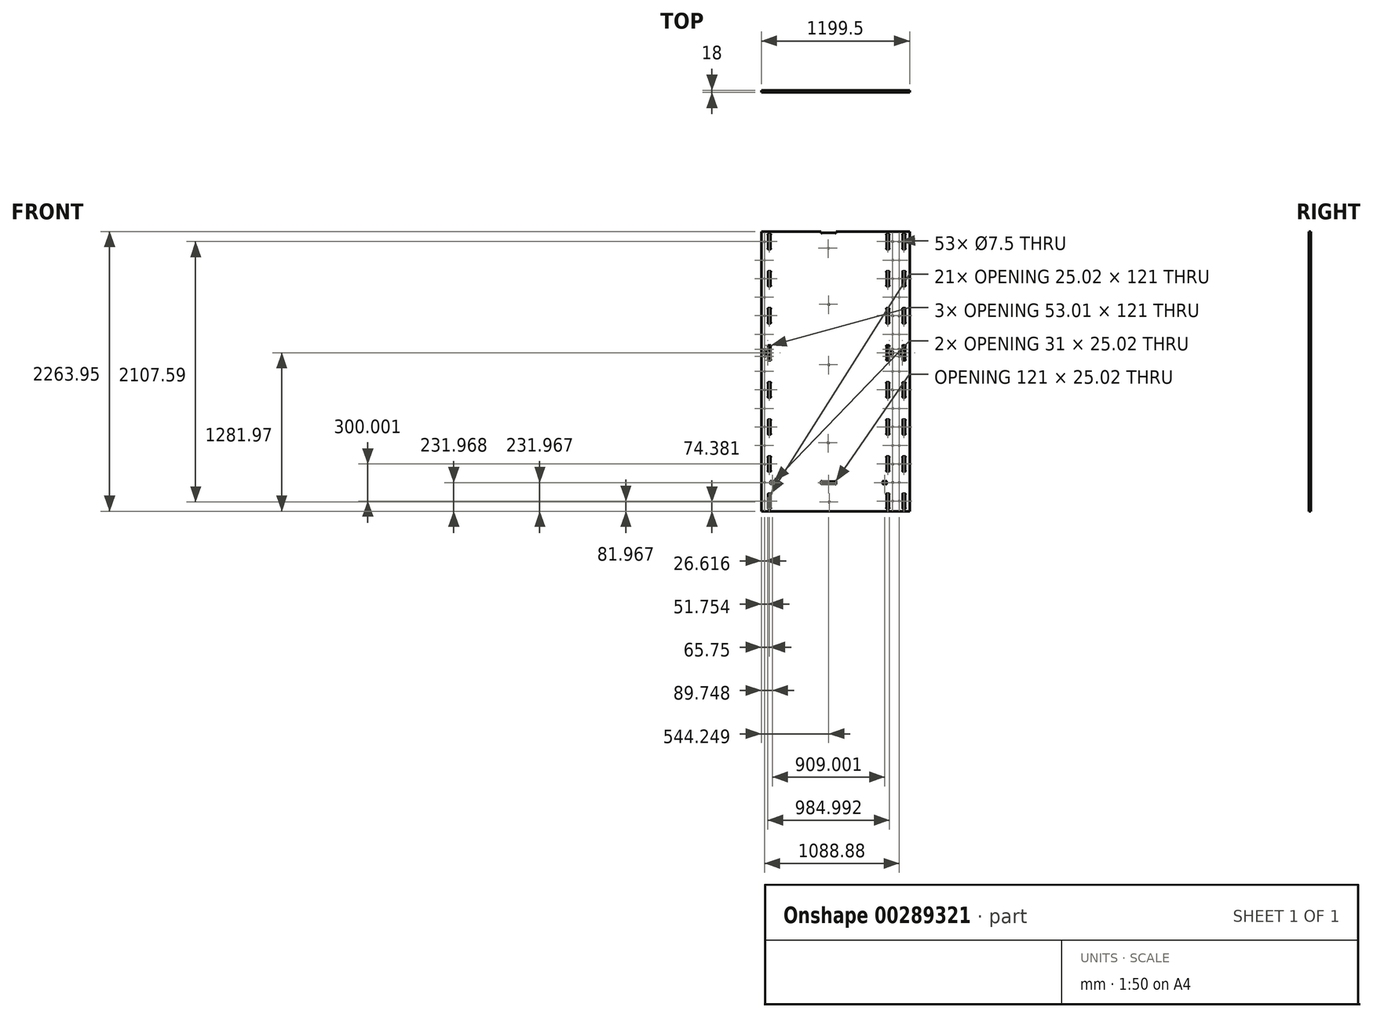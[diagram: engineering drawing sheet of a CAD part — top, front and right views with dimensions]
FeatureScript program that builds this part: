
annotation { "Feature Type Name" : "Feature", "Feature Type Description" : "" }
export const myFeature = defineFeature(function(context is Context, id is Id, definition is map)
    precondition{}
    {
        {
            var Q0;
            Q0=qCreatedBy(makeId("Front.planeOp"),FACE);
            var sketch = newSketch(context, id + "F0", { "sketchPlane" : qUnion([Q0])});
            skLineSegment(sketch, "E0", {"start": v(-600, -1200) * mm, "end": v(600, -1200) * mm});
            skLineSegment(sketch, "E1", {"start": v(600, -1200) * mm, "end": v(600, 1200) * mm});
            skLineSegment(sketch, "E2", {"start": v(600, 1200) * mm, "end": v(-600, 1200) * mm});
            skLineSegment(sketch, "E3", {"start": v(-600, 1200) * mm, "end": v(-600, -1200) * mm});
            skLineSegment(sketch, "E4", {"start": v(599.5, -1200) * mm, "end": v(599.5, 1063.95) * mm});
            skLineSegment(sketch, "E5", {"start": v(599.5, 1063.95) * mm, "end": v(4.5, 1063.95) * mm});
            skLineSegment(sketch, "E6", {"start": v(4.5, 1063.95) * mm, "end": v(4.5, 1053.8) * mm});
            skArc(sketch, "E7", {"start": v(4.5, 1053.8) * mm, "mid": v(1.36, 1050.55) * mm, "end": v(-2.02, 1053.56) * mm});
            skLineSegment(sketch, "E8", {"start": v(-2.02, 1053.56) * mm, "end": v(-109.48, 1053.56) * mm});
            skArc(sketch, "E9", {"start": v(-109.48, 1053.56) * mm, "mid": v(-112.86, 1050.54) * mm, "end": v(-116, 1053.8) * mm});
            skLineSegment(sketch, "E10", {"start": v(-116, 1053.8) * mm, "end": v(-116, 1063.95) * mm});
            skLineSegment(sketch, "E11", {"start": v(-116, 1063.95) * mm, "end": v(-600, 1063.95) * mm});
            skArc(sketch, "E12", {"start": v(564.25, -164.04) * mm, "mid": v(567.26, -160.66) * mm, "end": v(564, -157.53) * mm});
            skLineSegment(sketch, "E13", {"start": v(564, -157.53) * mm, "end": v(545.5, -157.53) * mm});
            skArc(sketch, "E14", {"start": v(545.5, -157.53) * mm, "mid": v(542.24, -160.66) * mm, "end": v(545.25, -164.04) * mm});
            skLineSegment(sketch, "E15", {"start": v(545.25, -164.04) * mm, "end": v(545.25, -272.02) * mm});
            skArc(sketch, "E16", {"start": v(545.25, -272.02) * mm, "mid": v(542.24, -275.4) * mm, "end": v(545.5, -278.53) * mm});
            skLineSegment(sketch, "E17", {"start": v(545.5, -278.53) * mm, "end": v(564, -278.53) * mm});
            skArc(sketch, "E18", {"start": v(564, -278.53) * mm, "mid": v(567.26, -275.4) * mm, "end": v(564.25, -272.02) * mm});
            skLineSegment(sketch, "E19", {"start": v(564.25, -272.02) * mm, "end": v(564.25, -164.04) * mm});
            skArc(sketch, "E20", {"start": v(432.25, -164.04) * mm, "mid": v(435.26, -160.66) * mm, "end": v(432, -157.53) * mm});
            skLineSegment(sketch, "E21", {"start": v(432, -157.53) * mm, "end": v(413.5, -157.53) * mm});
            skArc(sketch, "E22", {"start": v(413.5, -157.53) * mm, "mid": v(410.24, -160.66) * mm, "end": v(413.25, -164.04) * mm});
            skLineSegment(sketch, "E23", {"start": v(413.25, -164.04) * mm, "end": v(413.25, -272.02) * mm});
            skArc(sketch, "E24", {"start": v(413.25, -272.02) * mm, "mid": v(410.24, -275.4) * mm, "end": v(413.5, -278.53) * mm});
            skLineSegment(sketch, "E25", {"start": v(413.5, -278.53) * mm, "end": v(432, -278.53) * mm});
            skArc(sketch, "E26", {"start": v(432, -278.53) * mm, "mid": v(435.26, -275.4) * mm, "end": v(432.25, -272.02) * mm});
            skLineSegment(sketch, "E27", {"start": v(432.25, -272.02) * mm, "end": v(432.25, -164.04) * mm});
            skArc(sketch, "E28", {"start": v(432, 21.47) * mm, "mid": v(435.26, 24.6) * mm, "end": v(432.25, 27.98) * mm});
            skLineSegment(sketch, "E29", {"start": v(432.25, 27.98) * mm, "end": v(432.25, 72.47) * mm});
            skLineSegment(sketch, "E30", {"start": v(432.25, 72.47) * mm, "end": v(456.74, 72.47) * mm});
            skArc(sketch, "E31", {"start": v(456.74, 72.47) * mm, "mid": v(460.12, 69.46) * mm, "end": v(463.25, 72.72) * mm});
            skLineSegment(sketch, "E32", {"start": v(463.25, 72.72) * mm, "end": v(463.25, 91.22) * mm});
            skArc(sketch, "E33", {"start": v(463.25, 91.22) * mm, "mid": v(460.12, 94.48) * mm, "end": v(456.74, 91.47) * mm});
            skLineSegment(sketch, "E34", {"start": v(456.74, 91.47) * mm, "end": v(432.25, 91.47) * mm});
            skLineSegment(sketch, "E35", {"start": v(432.25, 91.47) * mm, "end": v(432.25, 135.96) * mm});
            skArc(sketch, "E36", {"start": v(432.25, 135.96) * mm, "mid": v(435.26, 139.33) * mm, "end": v(432, 142.47) * mm});
            skLineSegment(sketch, "E37", {"start": v(432, 142.47) * mm, "end": v(413.5, 142.47) * mm});
            skArc(sketch, "E38", {"start": v(413.5, 142.47) * mm, "mid": v(410.24, 139.33) * mm, "end": v(413.25, 135.96) * mm});
            skLineSegment(sketch, "E39", {"start": v(413.25, 135.96) * mm, "end": v(413.25, 27.98) * mm});
            skArc(sketch, "E40", {"start": v(413.25, 27.98) * mm, "mid": v(410.24, 24.6) * mm, "end": v(413.5, 21.47) * mm});
            skLineSegment(sketch, "E41", {"start": v(413.5, 21.47) * mm, "end": v(432, 21.47) * mm});
            skArc(sketch, "E42", {"start": v(432, 321.47) * mm, "mid": v(435.26, 324.6) * mm, "end": v(432.25, 327.99) * mm});
            skLineSegment(sketch, "E43", {"start": v(432.25, 327.99) * mm, "end": v(432.25, 435.96) * mm});
            skArc(sketch, "E44", {"start": v(432.25, 435.96) * mm, "mid": v(435.26, 439.34) * mm, "end": v(432, 442.47) * mm});
            skLineSegment(sketch, "E45", {"start": v(432, 442.47) * mm, "end": v(413.5, 442.47) * mm});
            skArc(sketch, "E46", {"start": v(413.5, 442.47) * mm, "mid": v(410.24, 439.34) * mm, "end": v(413.25, 435.96) * mm});
            skLineSegment(sketch, "E47", {"start": v(413.25, 435.96) * mm, "end": v(413.25, 327.99) * mm});
            skArc(sketch, "E48", {"start": v(413.25, 327.99) * mm, "mid": v(410.24, 324.6) * mm, "end": v(413.5, 321.47) * mm});
            skLineSegment(sketch, "E49", {"start": v(413.5, 321.47) * mm, "end": v(432, 321.47) * mm});
            skArc(sketch, "E50", {"start": v(432, 621.47) * mm, "mid": v(435.26, 624.61) * mm, "end": v(432.25, 627.99) * mm});
            skLineSegment(sketch, "E51", {"start": v(432.25, 627.99) * mm, "end": v(432.25, 735.96) * mm});
            skArc(sketch, "E52", {"start": v(432.25, 735.96) * mm, "mid": v(435.26, 739.34) * mm, "end": v(432, 742.47) * mm});
            skLineSegment(sketch, "E53", {"start": v(432, 742.47) * mm, "end": v(413.5, 742.47) * mm});
            skArc(sketch, "E54", {"start": v(413.5, 742.47) * mm, "mid": v(410.24, 739.34) * mm, "end": v(413.25, 735.96) * mm});
            skLineSegment(sketch, "E55", {"start": v(413.25, 735.96) * mm, "end": v(413.25, 627.99) * mm});
            skArc(sketch, "E56", {"start": v(413.25, 627.99) * mm, "mid": v(410.24, 624.61) * mm, "end": v(413.5, 621.47) * mm});
            skLineSegment(sketch, "E57", {"start": v(413.5, 621.47) * mm, "end": v(432, 621.47) * mm});
            skArc(sketch, "E58", {"start": v(-524.75, 435.96) * mm, "mid": v(-521.74, 439.33) * mm, "end": v(-525, 442.47) * mm});
            skLineSegment(sketch, "E59", {"start": v(-525, 442.47) * mm, "end": v(-543.5, 442.47) * mm});
            skArc(sketch, "E60", {"start": v(-543.5, 442.47) * mm, "mid": v(-546.76, 439.33) * mm, "end": v(-543.75, 435.96) * mm});
            skLineSegment(sketch, "E61", {"start": v(-543.75, 435.96) * mm, "end": v(-543.75, 327.98) * mm});
            skArc(sketch, "E62", {"start": v(-543.75, 327.98) * mm, "mid": v(-546.76, 324.6) * mm, "end": v(-543.5, 321.47) * mm});
            skLineSegment(sketch, "E63", {"start": v(-543.5, 321.47) * mm, "end": v(-525, 321.47) * mm});
            skArc(sketch, "E64", {"start": v(-525, 321.47) * mm, "mid": v(-521.74, 324.6) * mm, "end": v(-524.75, 327.98) * mm});
            skLineSegment(sketch, "E65", {"start": v(-524.75, 327.98) * mm, "end": v(-524.75, 435.96) * mm});
            skArc(sketch, "E66", {"start": v(-524.75, 135.96) * mm, "mid": v(-521.74, 139.33) * mm, "end": v(-525, 142.47) * mm});
            skLineSegment(sketch, "E67", {"start": v(-525, 142.47) * mm, "end": v(-543.5, 142.47) * mm});
            skArc(sketch, "E68", {"start": v(-543.5, 142.47) * mm, "mid": v(-546.76, 139.33) * mm, "end": v(-543.75, 135.96) * mm});
            skLineSegment(sketch, "E69", {"start": v(-543.75, 135.96) * mm, "end": v(-543.75, 91.47) * mm});
            skLineSegment(sketch, "E70", {"start": v(-543.75, 91.47) * mm, "end": v(-568.24, 91.47) * mm});
            skArc(sketch, "E71", {"start": v(-568.24, 91.47) * mm, "mid": v(-571.61, 94.48) * mm, "end": v(-574.75, 91.22) * mm});
            skLineSegment(sketch, "E72", {"start": v(-574.75, 91.22) * mm, "end": v(-574.75, 72.72) * mm});
            skArc(sketch, "E73", {"start": v(-574.75, 72.72) * mm, "mid": v(-571.61, 69.46) * mm, "end": v(-568.24, 72.47) * mm});
            skLineSegment(sketch, "E74", {"start": v(-568.24, 72.47) * mm, "end": v(-543.75, 72.47) * mm});
            skLineSegment(sketch, "E75", {"start": v(-543.75, 72.47) * mm, "end": v(-543.75, 27.98) * mm});
            skArc(sketch, "E76", {"start": v(-543.75, 27.98) * mm, "mid": v(-546.76, 24.6) * mm, "end": v(-543.5, 21.47) * mm});
            skLineSegment(sketch, "E77", {"start": v(-543.5, 21.47) * mm, "end": v(-525, 21.47) * mm});
            skArc(sketch, "E78", {"start": v(-525, 21.47) * mm, "mid": v(-521.74, 24.6) * mm, "end": v(-524.75, 27.98) * mm});
            skLineSegment(sketch, "E79", {"start": v(-524.75, 27.98) * mm, "end": v(-524.75, 135.96) * mm});
            skArc(sketch, "E80", {"start": v(-524.75, -164.04) * mm, "mid": v(-521.74, -160.67) * mm, "end": v(-525, -157.53) * mm});
            skLineSegment(sketch, "E81", {"start": v(-525, -157.53) * mm, "end": v(-543.5, -157.53) * mm});
            skArc(sketch, "E82", {"start": v(-543.5, -157.53) * mm, "mid": v(-546.76, -160.67) * mm, "end": v(-543.75, -164.04) * mm});
            skLineSegment(sketch, "E83", {"start": v(-543.75, -164.04) * mm, "end": v(-543.75, -272.02) * mm});
            skArc(sketch, "E84", {"start": v(-543.75, -272.02) * mm, "mid": v(-546.76, -275.4) * mm, "end": v(-543.5, -278.53) * mm});
            skLineSegment(sketch, "E85", {"start": v(-543.5, -278.53) * mm, "end": v(-525, -278.53) * mm});
            skArc(sketch, "E86", {"start": v(-525, -278.53) * mm, "mid": v(-521.74, -275.4) * mm, "end": v(-524.75, -272.02) * mm});
            skLineSegment(sketch, "E87", {"start": v(-524.75, -272.02) * mm, "end": v(-524.75, -164.04) * mm});
            skArc(sketch, "E88", {"start": v(-524.75, -464.04) * mm, "mid": v(-521.74, -460.67) * mm, "end": v(-525, -457.53) * mm});
            skLineSegment(sketch, "E89", {"start": v(-525, -457.53) * mm, "end": v(-543.5, -457.53) * mm});
            skArc(sketch, "E90", {"start": v(-543.5, -457.53) * mm, "mid": v(-546.76, -460.67) * mm, "end": v(-543.75, -464.04) * mm});
            skLineSegment(sketch, "E91", {"start": v(-543.75, -464.04) * mm, "end": v(-543.75, -572.02) * mm});
            skArc(sketch, "E92", {"start": v(-543.75, -572.02) * mm, "mid": v(-546.76, -575.4) * mm, "end": v(-543.5, -578.53) * mm});
            skLineSegment(sketch, "E93", {"start": v(-543.5, -578.53) * mm, "end": v(-525, -578.53) * mm});
            skArc(sketch, "E94", {"start": v(-525, -578.53) * mm, "mid": v(-521.74, -575.4) * mm, "end": v(-524.75, -572.02) * mm});
            skLineSegment(sketch, "E95", {"start": v(-524.75, -572.02) * mm, "end": v(-524.75, -464.04) * mm});
            skArc(sketch, "E96", {"start": v(-524.75, -764.04) * mm, "mid": v(-521.74, -760.67) * mm, "end": v(-525, -757.53) * mm});
            skLineSegment(sketch, "E97", {"start": v(-525, -757.53) * mm, "end": v(-543.5, -757.53) * mm});
            skArc(sketch, "E98", {"start": v(-543.5, -757.53) * mm, "mid": v(-546.76, -760.67) * mm, "end": v(-543.75, -764.04) * mm});
            skLineSegment(sketch, "E99", {"start": v(-543.75, -764.04) * mm, "end": v(-543.75, -872.02) * mm});
            skArc(sketch, "E100", {"start": v(-543.75, -872.02) * mm, "mid": v(-546.76, -875.4) * mm, "end": v(-543.5, -878.53) * mm});
            skLineSegment(sketch, "E101", {"start": v(-543.5, -878.53) * mm, "end": v(-525, -878.53) * mm});
            skArc(sketch, "E102", {"start": v(-525, -878.53) * mm, "mid": v(-521.74, -875.4) * mm, "end": v(-524.75, -872.02) * mm});
            skLineSegment(sketch, "E103", {"start": v(-524.75, -872.02) * mm, "end": v(-524.75, -764.04) * mm});
            skArc(sketch, "E104", {"start": v(-519.24, -958.53) * mm, "mid": v(-522.62, -955.52) * mm, "end": v(-525.75, -958.78) * mm});
            skLineSegment(sketch, "E105", {"start": v(-525.75, -958.78) * mm, "end": v(-525.75, -977.28) * mm});
            skArc(sketch, "E106", {"start": v(-525.75, -977.28) * mm, "mid": v(-522.62, -980.54) * mm, "end": v(-519.24, -977.53) * mm});
            skLineSegment(sketch, "E107", {"start": v(-519.24, -977.53) * mm, "end": v(-501.26, -977.53) * mm});
            skArc(sketch, "E108", {"start": v(-501.26, -977.53) * mm, "mid": v(-497.89, -980.54) * mm, "end": v(-494.75, -977.28) * mm});
            skLineSegment(sketch, "E109", {"start": v(-494.75, -977.28) * mm, "end": v(-494.75, -958.78) * mm});
            skArc(sketch, "E110", {"start": v(-494.75, -958.78) * mm, "mid": v(-497.89, -955.52) * mm, "end": v(-501.26, -958.53) * mm});
            skLineSegment(sketch, "E111", {"start": v(-501.26, -958.53) * mm, "end": v(-519.24, -958.53) * mm});
            skArc(sketch, "E112", {"start": v(-116.25, -977.28) * mm, "mid": v(-113.12, -980.54) * mm, "end": v(-109.74, -977.53) * mm});
            skLineSegment(sketch, "E113", {"start": v(-109.74, -977.53) * mm, "end": v(-1.76, -977.53) * mm});
            skArc(sketch, "E114", {"start": v(-1.76, -977.53) * mm, "mid": v(1.61, -980.54) * mm, "end": v(4.75, -977.28) * mm});
            skLineSegment(sketch, "E115", {"start": v(4.75, -977.28) * mm, "end": v(4.75, -958.78) * mm});
            skArc(sketch, "E116", {"start": v(4.75, -958.78) * mm, "mid": v(1.61, -955.52) * mm, "end": v(-1.76, -958.53) * mm});
            skLineSegment(sketch, "E117", {"start": v(-1.76, -958.53) * mm, "end": v(-109.74, -958.53) * mm});
            skArc(sketch, "E118", {"start": v(-109.74, -958.53) * mm, "mid": v(-113.12, -955.52) * mm, "end": v(-116.25, -958.78) * mm});
            skLineSegment(sketch, "E119", {"start": v(-116.25, -958.78) * mm, "end": v(-116.25, -977.28) * mm});
            skArc(sketch, "E120", {"start": v(383.25, -977.28) * mm, "mid": v(386.38, -980.54) * mm, "end": v(389.76, -977.53) * mm});
            skLineSegment(sketch, "E121", {"start": v(389.76, -977.53) * mm, "end": v(407.74, -977.53) * mm});
            skArc(sketch, "E122", {"start": v(407.74, -977.53) * mm, "mid": v(411.11, -980.54) * mm, "end": v(414.25, -977.28) * mm});
            skLineSegment(sketch, "E123", {"start": v(414.25, -977.28) * mm, "end": v(414.25, -958.78) * mm});
            skArc(sketch, "E124", {"start": v(414.25, -958.78) * mm, "mid": v(411.11, -955.52) * mm, "end": v(407.74, -958.53) * mm});
            skLineSegment(sketch, "E125", {"start": v(407.74, -958.53) * mm, "end": v(389.76, -958.53) * mm});
            skArc(sketch, "E126", {"start": v(389.76, -958.53) * mm, "mid": v(386.38, -955.52) * mm, "end": v(383.25, -958.78) * mm});
            skLineSegment(sketch, "E127", {"start": v(383.25, -958.78) * mm, "end": v(383.25, -977.28) * mm});
            skArc(sketch, "E128", {"start": v(545.25, -872.02) * mm, "mid": v(542.24, -875.4) * mm, "end": v(545.5, -878.53) * mm});
            skLineSegment(sketch, "E129", {"start": v(545.5, -878.53) * mm, "end": v(564, -878.53) * mm});
            skArc(sketch, "E130", {"start": v(564, -878.53) * mm, "mid": v(567.26, -875.4) * mm, "end": v(564.25, -872.02) * mm});
            skLineSegment(sketch, "E131", {"start": v(564.25, -872.02) * mm, "end": v(564.25, -764.04) * mm});
            skArc(sketch, "E132", {"start": v(564.25, -764.04) * mm, "mid": v(567.26, -760.66) * mm, "end": v(564, -757.53) * mm});
            skLineSegment(sketch, "E133", {"start": v(564, -757.53) * mm, "end": v(545.5, -757.53) * mm});
            skArc(sketch, "E134", {"start": v(545.5, -757.53) * mm, "mid": v(542.24, -760.66) * mm, "end": v(545.25, -764.04) * mm});
            skLineSegment(sketch, "E135", {"start": v(545.25, -764.04) * mm, "end": v(545.25, -872.02) * mm});
            skArc(sketch, "E136", {"start": v(432.25, -764.04) * mm, "mid": v(435.26, -760.66) * mm, "end": v(432, -757.53) * mm});
            skLineSegment(sketch, "E137", {"start": v(432, -757.53) * mm, "end": v(413.5, -757.53) * mm});
            skArc(sketch, "E138", {"start": v(413.5, -757.53) * mm, "mid": v(410.24, -760.66) * mm, "end": v(413.25, -764.04) * mm});
            skLineSegment(sketch, "E139", {"start": v(413.25, -764.04) * mm, "end": v(413.25, -872.02) * mm});
            skArc(sketch, "E140", {"start": v(413.25, -872.02) * mm, "mid": v(410.24, -875.4) * mm, "end": v(413.5, -878.53) * mm});
            skLineSegment(sketch, "E141", {"start": v(413.5, -878.53) * mm, "end": v(432, -878.53) * mm});
            skArc(sketch, "E142", {"start": v(432, -878.53) * mm, "mid": v(435.26, -875.4) * mm, "end": v(432.25, -872.02) * mm});
            skLineSegment(sketch, "E143", {"start": v(432.25, -872.02) * mm, "end": v(432.25, -764.04) * mm});
            skArc(sketch, "E144", {"start": v(432, -578.53) * mm, "mid": v(435.26, -575.4) * mm, "end": v(432.25, -572.02) * mm});
            skLineSegment(sketch, "E145", {"start": v(432.25, -572.02) * mm, "end": v(432.25, -464.04) * mm});
            skArc(sketch, "E146", {"start": v(432.25, -464.04) * mm, "mid": v(435.26, -460.66) * mm, "end": v(432, -457.53) * mm});
            skLineSegment(sketch, "E147", {"start": v(432, -457.53) * mm, "end": v(413.5, -457.53) * mm});
            skArc(sketch, "E148", {"start": v(413.5, -457.53) * mm, "mid": v(410.24, -460.66) * mm, "end": v(413.25, -464.04) * mm});
            skLineSegment(sketch, "E149", {"start": v(413.25, -464.04) * mm, "end": v(413.25, -572.02) * mm});
            skArc(sketch, "E150", {"start": v(413.25, -572.02) * mm, "mid": v(410.24, -575.4) * mm, "end": v(413.5, -578.53) * mm});
            skLineSegment(sketch, "E151", {"start": v(413.5, -578.53) * mm, "end": v(432, -578.53) * mm});
            skArc(sketch, "E152", {"start": v(545.25, -572.02) * mm, "mid": v(542.24, -575.4) * mm, "end": v(545.5, -578.53) * mm});
            skLineSegment(sketch, "E153", {"start": v(545.5, -578.53) * mm, "end": v(564, -578.53) * mm});
            skArc(sketch, "E154", {"start": v(564, -578.53) * mm, "mid": v(567.26, -575.4) * mm, "end": v(564.25, -572.02) * mm});
            skLineSegment(sketch, "E155", {"start": v(564.25, -572.02) * mm, "end": v(564.25, -464.04) * mm});
            skArc(sketch, "E156", {"start": v(564.25, -464.04) * mm, "mid": v(567.26, -460.66) * mm, "end": v(564, -457.53) * mm});
            skLineSegment(sketch, "E157", {"start": v(564, -457.53) * mm, "end": v(545.5, -457.53) * mm});
            skArc(sketch, "E158", {"start": v(545.5, -457.53) * mm, "mid": v(542.24, -460.66) * mm, "end": v(545.25, -464.04) * mm});
            skLineSegment(sketch, "E159", {"start": v(545.25, -464.04) * mm, "end": v(545.25, -572.02) * mm});
            skArc(sketch, "E160", {"start": v(413.5, -1057.54) * mm, "mid": v(410.24, -1060.67) * mm, "end": v(413.25, -1064.05) * mm});
            skLineSegment(sketch, "E161", {"start": v(413.25, -1064.05) * mm, "end": v(413.25, -1172.03) * mm});
            skArc(sketch, "E162", {"start": v(413.25, -1172.03) * mm, "mid": v(410.24, -1175.4) * mm, "end": v(413.5, -1178.54) * mm});
            skLineSegment(sketch, "E163", {"start": v(413.5, -1178.54) * mm, "end": v(432, -1178.54) * mm});
            skArc(sketch, "E164", {"start": v(432, -1178.54) * mm, "mid": v(435.26, -1175.4) * mm, "end": v(432.25, -1172.03) * mm});
            skLineSegment(sketch, "E165", {"start": v(432.25, -1172.03) * mm, "end": v(432.25, -1064.05) * mm});
            skArc(sketch, "E166", {"start": v(432.25, -1064.05) * mm, "mid": v(435.26, -1060.67) * mm, "end": v(432, -1057.54) * mm});
            skLineSegment(sketch, "E167", {"start": v(432, -1057.54) * mm, "end": v(413.5, -1057.54) * mm});
            skLineSegment(sketch, "E168", {"start": v(545.25, -1064.05) * mm, "end": v(545.25, -1172.03) * mm});
            skArc(sketch, "E169", {"start": v(545.25, -1172.03) * mm, "mid": v(542.24, -1175.4) * mm, "end": v(545.5, -1178.54) * mm});
            skLineSegment(sketch, "E170", {"start": v(545.5, -1178.54) * mm, "end": v(564, -1178.54) * mm});
            skArc(sketch, "E171", {"start": v(564, -1178.54) * mm, "mid": v(567.26, -1175.4) * mm, "end": v(564.25, -1172.03) * mm});
            skLineSegment(sketch, "E172", {"start": v(564.25, -1172.03) * mm, "end": v(564.25, -1064.05) * mm});
            skArc(sketch, "E173", {"start": v(564.25, -1064.05) * mm, "mid": v(567.26, -1060.67) * mm, "end": v(564, -1057.54) * mm});
            skLineSegment(sketch, "E174", {"start": v(564, -1057.54) * mm, "end": v(545.5, -1057.54) * mm});
            skArc(sketch, "E175", {"start": v(545.5, -1057.54) * mm, "mid": v(542.24, -1060.67) * mm, "end": v(545.25, -1064.05) * mm});
            skArc(sketch, "E176", {"start": v(-543.5, -1057.53) * mm, "mid": v(-546.76, -1060.67) * mm, "end": v(-543.75, -1064.04) * mm});
            skLineSegment(sketch, "E177", {"start": v(-543.75, -1064.04) * mm, "end": v(-543.75, -1172.02) * mm});
            skArc(sketch, "E178", {"start": v(-543.75, -1172.02) * mm, "mid": v(-546.76, -1175.4) * mm, "end": v(-543.5, -1178.53) * mm});
            skLineSegment(sketch, "E179", {"start": v(-543.5, -1178.53) * mm, "end": v(-525, -1178.53) * mm});
            skArc(sketch, "E180", {"start": v(-525, -1178.53) * mm, "mid": v(-521.74, -1175.4) * mm, "end": v(-524.75, -1172.02) * mm});
            skLineSegment(sketch, "E181", {"start": v(-524.75, -1172.02) * mm, "end": v(-524.75, -1064.04) * mm});
            skArc(sketch, "E182", {"start": v(-524.75, -1064.04) * mm, "mid": v(-521.74, -1060.67) * mm, "end": v(-525, -1057.53) * mm});
            skLineSegment(sketch, "E183", {"start": v(-525, -1057.53) * mm, "end": v(-543.5, -1057.53) * mm});
            skArc(sketch, "E184", {"start": v(-525, 621.47) * mm, "mid": v(-521.74, 624.6) * mm, "end": v(-524.75, 627.98) * mm});
            skLineSegment(sketch, "E185", {"start": v(-524.75, 627.98) * mm, "end": v(-524.75, 735.96) * mm});
            skArc(sketch, "E186", {"start": v(-524.75, 735.96) * mm, "mid": v(-521.74, 739.33) * mm, "end": v(-525, 742.47) * mm});
            skLineSegment(sketch, "E187", {"start": v(-525, 742.47) * mm, "end": v(-543.5, 742.47) * mm});
            skArc(sketch, "E188", {"start": v(-543.5, 742.47) * mm, "mid": v(-546.76, 739.33) * mm, "end": v(-543.75, 735.96) * mm});
            skLineSegment(sketch, "E189", {"start": v(-543.75, 735.96) * mm, "end": v(-543.75, 627.98) * mm});
            skArc(sketch, "E190", {"start": v(-543.75, 627.98) * mm, "mid": v(-546.76, 624.6) * mm, "end": v(-543.5, 621.47) * mm});
            skLineSegment(sketch, "E191", {"start": v(-543.5, 621.47) * mm, "end": v(-525, 621.47) * mm});
            skArc(sketch, "E192", {"start": v(-525, 921.47) * mm, "mid": v(-521.74, 924.6) * mm, "end": v(-524.75, 927.98) * mm});
            skLineSegment(sketch, "E193", {"start": v(-524.75, 927.98) * mm, "end": v(-524.75, 1035.96) * mm});
            skArc(sketch, "E194", {"start": v(-524.75, 1035.96) * mm, "mid": v(-521.74, 1039.34) * mm, "end": v(-525, 1042.47) * mm});
            skLineSegment(sketch, "E195", {"start": v(-525, 1042.47) * mm, "end": v(-543.5, 1042.47) * mm});
            skArc(sketch, "E196", {"start": v(-543.5, 1042.47) * mm, "mid": v(-546.76, 1039.34) * mm, "end": v(-543.75, 1035.96) * mm});
            skLineSegment(sketch, "E197", {"start": v(-543.75, 1035.96) * mm, "end": v(-543.75, 927.98) * mm});
            skArc(sketch, "E198", {"start": v(-543.75, 927.98) * mm, "mid": v(-546.76, 924.6) * mm, "end": v(-543.5, 921.47) * mm});
            skLineSegment(sketch, "E199", {"start": v(-543.5, 921.47) * mm, "end": v(-525, 921.47) * mm});
            skArc(sketch, "E200", {"start": v(432, 921.47) * mm, "mid": v(435.26, 924.6) * mm, "end": v(432.25, 927.99) * mm});
            skLineSegment(sketch, "E201", {"start": v(432.25, 927.99) * mm, "end": v(432.25, 1035.96) * mm});
            skArc(sketch, "E202", {"start": v(432.25, 1035.96) * mm, "mid": v(435.26, 1039.34) * mm, "end": v(432, 1042.47) * mm});
            skLineSegment(sketch, "E203", {"start": v(432, 1042.47) * mm, "end": v(413.5, 1042.47) * mm});
            skArc(sketch, "E204", {"start": v(413.5, 1042.47) * mm, "mid": v(410.24, 1039.34) * mm, "end": v(413.25, 1035.96) * mm});
            skLineSegment(sketch, "E205", {"start": v(413.25, 1035.96) * mm, "end": v(413.25, 927.99) * mm});
            skArc(sketch, "E206", {"start": v(413.25, 927.99) * mm, "mid": v(410.24, 924.6) * mm, "end": v(413.5, 921.47) * mm});
            skLineSegment(sketch, "E207", {"start": v(413.5, 921.47) * mm, "end": v(432, 921.47) * mm});
            skArc(sketch, "E208", {"start": v(545.25, 927.99) * mm, "mid": v(542.24, 924.61) * mm, "end": v(545.5, 921.47) * mm});
            skLineSegment(sketch, "E209", {"start": v(545.5, 921.47) * mm, "end": v(564, 921.47) * mm});
            skArc(sketch, "E210", {"start": v(564, 921.47) * mm, "mid": v(567.26, 924.61) * mm, "end": v(564.25, 927.99) * mm});
            skLineSegment(sketch, "E211", {"start": v(564.25, 927.99) * mm, "end": v(564.25, 1035.96) * mm});
            skArc(sketch, "E212", {"start": v(564.25, 1035.96) * mm, "mid": v(567.26, 1039.34) * mm, "end": v(564, 1042.47) * mm});
            skLineSegment(sketch, "E213", {"start": v(564, 1042.47) * mm, "end": v(545.5, 1042.47) * mm});
            skArc(sketch, "E214", {"start": v(545.5, 1042.47) * mm, "mid": v(542.24, 1039.34) * mm, "end": v(545.25, 1035.96) * mm});
            skLineSegment(sketch, "E215", {"start": v(545.25, 1035.96) * mm, "end": v(545.25, 927.99) * mm});
            skArc(sketch, "E216", {"start": v(545.25, 627.99) * mm, "mid": v(542.24, 624.6) * mm, "end": v(545.5, 621.47) * mm});
            skLineSegment(sketch, "E217", {"start": v(545.5, 621.47) * mm, "end": v(564, 621.47) * mm});
            skArc(sketch, "E218", {"start": v(564, 621.47) * mm, "mid": v(567.26, 624.6) * mm, "end": v(564.25, 627.99) * mm});
            skLineSegment(sketch, "E219", {"start": v(564.25, 627.99) * mm, "end": v(564.25, 735.96) * mm});
            skArc(sketch, "E220", {"start": v(564.25, 735.96) * mm, "mid": v(567.26, 739.34) * mm, "end": v(564, 742.47) * mm});
            skLineSegment(sketch, "E221", {"start": v(564, 742.47) * mm, "end": v(545.5, 742.47) * mm});
            skArc(sketch, "E222", {"start": v(545.5, 742.47) * mm, "mid": v(542.24, 739.34) * mm, "end": v(545.25, 735.96) * mm});
            skLineSegment(sketch, "E223", {"start": v(545.25, 735.96) * mm, "end": v(545.25, 627.99) * mm});
            skArc(sketch, "E224", {"start": v(545.25, 327.99) * mm, "mid": v(542.24, 324.6) * mm, "end": v(545.5, 321.47) * mm});
            skLineSegment(sketch, "E225", {"start": v(545.5, 321.47) * mm, "end": v(564, 321.47) * mm});
            skArc(sketch, "E226", {"start": v(564, 321.47) * mm, "mid": v(567.26, 324.6) * mm, "end": v(564.25, 327.99) * mm});
            skLineSegment(sketch, "E227", {"start": v(564.25, 327.99) * mm, "end": v(564.25, 435.96) * mm});
            skArc(sketch, "E228", {"start": v(564.25, 435.96) * mm, "mid": v(567.26, 439.34) * mm, "end": v(564, 442.47) * mm});
            skLineSegment(sketch, "E229", {"start": v(564, 442.47) * mm, "end": v(545.5, 442.47) * mm});
            skArc(sketch, "E230", {"start": v(545.5, 442.47) * mm, "mid": v(542.24, 439.34) * mm, "end": v(545.25, 435.96) * mm});
            skLineSegment(sketch, "E231", {"start": v(545.25, 435.96) * mm, "end": v(545.25, 327.99) * mm});
            skArc(sketch, "E232", {"start": v(545.25, 27.98) * mm, "mid": v(542.24, 24.6) * mm, "end": v(545.5, 21.47) * mm});
            skLineSegment(sketch, "E233", {"start": v(545.5, 21.47) * mm, "end": v(564, 21.47) * mm});
            skArc(sketch, "E234", {"start": v(564, 21.47) * mm, "mid": v(567.26, 24.6) * mm, "end": v(564.25, 27.98) * mm});
            skLineSegment(sketch, "E235", {"start": v(564.25, 27.98) * mm, "end": v(564.25, 135.96) * mm});
            skArc(sketch, "E236", {"start": v(564.25, 135.96) * mm, "mid": v(567.26, 139.33) * mm, "end": v(564, 142.47) * mm});
            skLineSegment(sketch, "E237", {"start": v(564, 142.47) * mm, "end": v(545.5, 142.47) * mm});
            skArc(sketch, "E238", {"start": v(545.5, 142.47) * mm, "mid": v(542.24, 139.33) * mm, "end": v(545.25, 135.96) * mm});
            skLineSegment(sketch, "E239", {"start": v(545.25, 135.96) * mm, "end": v(545.25, 91.47) * mm});
            skLineSegment(sketch, "E240", {"start": v(545.25, 91.47) * mm, "end": v(520.76, 91.47) * mm});
            skArc(sketch, "E241", {"start": v(520.76, 91.47) * mm, "mid": v(517.39, 94.47) * mm, "end": v(514.25, 91.22) * mm});
            skLineSegment(sketch, "E242", {"start": v(514.25, 91.22) * mm, "end": v(514.25, 72.72) * mm});
            skArc(sketch, "E243", {"start": v(514.25, 72.72) * mm, "mid": v(517.39, 69.46) * mm, "end": v(520.76, 72.47) * mm});
            skLineSegment(sketch, "E244", {"start": v(520.76, 72.47) * mm, "end": v(545.25, 72.47) * mm});
            skLineSegment(sketch, "E245", {"start": v(545.25, 72.47) * mm, "end": v(545.25, 27.98) * mm});
            skLineSegment(sketch, "E246", {"start": v(-136.58, 92.99) * mm, "end": v(-136.58, 132.95) * mm});
            skLineSegment(sketch, "E247", {"start": v(-136.58, 132.95) * mm, "end": v(-119.02, 132.95) * mm});
            skLineSegment(sketch, "E248", {"start": v(-119.02, 132.95) * mm, "end": v(-118.53, 132.95) * mm});
            skLineSegment(sketch, "E249", {"start": v(-118.53, 132.95) * mm, "end": v(-118.03, 132.92) * mm});
            skLineSegment(sketch, "E250", {"start": v(-118.03, 132.92) * mm, "end": v(-117.55, 132.86) * mm});
            skLineSegment(sketch, "E251", {"start": v(-117.55, 132.86) * mm, "end": v(-117.06, 132.78) * mm});
            skLineSegment(sketch, "E252", {"start": v(-117.06, 132.78) * mm, "end": v(-116.59, 132.68) * mm});
            skLineSegment(sketch, "E253", {"start": v(-116.59, 132.68) * mm, "end": v(-116.12, 132.55) * mm});
            skLineSegment(sketch, "E254", {"start": v(-116.12, 132.55) * mm, "end": v(-115.65, 132.4) * mm});
            skLineSegment(sketch, "E255", {"start": v(-115.65, 132.4) * mm, "end": v(-115.2, 132.23) * mm});
            skLineSegment(sketch, "E256", {"start": v(-115.2, 132.23) * mm, "end": v(-114.75, 132.03) * mm});
            skLineSegment(sketch, "E257", {"start": v(-114.75, 132.03) * mm, "end": v(-114.32, 131.81) * mm});
            skLineSegment(sketch, "E258", {"start": v(-114.32, 131.81) * mm, "end": v(-113.9, 131.57) * mm});
            skLineSegment(sketch, "E259", {"start": v(-113.9, 131.57) * mm, "end": v(-113.48, 131.3) * mm});
            skLineSegment(sketch, "E260", {"start": v(-113.48, 131.3) * mm, "end": v(-113.08, 131.02) * mm});
            skLineSegment(sketch, "E261", {"start": v(-113.08, 131.02) * mm, "end": v(-112.7, 130.72) * mm});
            skLineSegment(sketch, "E262", {"start": v(-112.7, 130.72) * mm, "end": v(-112.33, 130.4) * mm});
            skLineSegment(sketch, "E263", {"start": v(-112.33, 130.4) * mm, "end": v(-111.98, 130.05) * mm});
            skLineSegment(sketch, "E264", {"start": v(-111.98, 130.05) * mm, "end": v(-111.64, 129.7) * mm});
            skLineSegment(sketch, "E265", {"start": v(-111.64, 129.7) * mm, "end": v(-111.32, 129.33) * mm});
            skLineSegment(sketch, "E266", {"start": v(-111.32, 129.33) * mm, "end": v(-111.01, 128.95) * mm});
            skLineSegment(sketch, "E267", {"start": v(-111.01, 128.95) * mm, "end": v(-110.73, 128.55) * mm});
            skLineSegment(sketch, "E268", {"start": v(-110.73, 128.55) * mm, "end": v(-110.47, 128.14) * mm});
            skLineSegment(sketch, "E269", {"start": v(-110.47, 128.14) * mm, "end": v(-110.23, 127.72) * mm});
            skLineSegment(sketch, "E270", {"start": v(-110.23, 127.72) * mm, "end": v(-110.01, 127.3) * mm});
            skLineSegment(sketch, "E271", {"start": v(-110.01, 127.3) * mm, "end": v(-109.82, 126.85) * mm});
            skLineSegment(sketch, "E272", {"start": v(-109.82, 126.85) * mm, "end": v(-109.64, 126.4) * mm});
            skLineSegment(sketch, "E273", {"start": v(-109.64, 126.4) * mm, "end": v(-109.49, 125.94) * mm});
            skLineSegment(sketch, "E274", {"start": v(-109.49, 125.94) * mm, "end": v(-109.36, 125.48) * mm});
            skLineSegment(sketch, "E275", {"start": v(-109.36, 125.48) * mm, "end": v(-109.25, 125) * mm});
            skLineSegment(sketch, "E276", {"start": v(-109.25, 125) * mm, "end": v(-109.17, 124.53) * mm});
            skLineSegment(sketch, "E277", {"start": v(-109.17, 124.53) * mm, "end": v(-109.1, 124.05) * mm});
            skLineSegment(sketch, "E278", {"start": v(-109.1, 124.05) * mm, "end": v(-109.07, 123.56) * mm});
            skLineSegment(sketch, "E279", {"start": v(-109.07, 123.56) * mm, "end": v(-109.06, 123.07) * mm});
            skLineSegment(sketch, "E280", {"start": v(-109.06, 123.07) * mm, "end": v(-109.06, 122.57) * mm});
            skLineSegment(sketch, "E281", {"start": v(-109.06, 122.57) * mm, "end": v(-109.08, 122.07) * mm});
            skLineSegment(sketch, "E282", {"start": v(-109.08, 122.07) * mm, "end": v(-109.13, 121.57) * mm});
            skLineSegment(sketch, "E283", {"start": v(-109.13, 121.57) * mm, "end": v(-109.2, 121.08) * mm});
            skLineSegment(sketch, "E284", {"start": v(-109.2, 121.08) * mm, "end": v(-109.3, 120.6) * mm});
            skLineSegment(sketch, "E285", {"start": v(-109.3, 120.6) * mm, "end": v(-109.42, 120.12) * mm});
            skLineSegment(sketch, "E286", {"start": v(-109.42, 120.12) * mm, "end": v(-109.57, 119.65) * mm});
            skLineSegment(sketch, "E287", {"start": v(-109.57, 119.65) * mm, "end": v(-109.74, 119.18) * mm});
            skLineSegment(sketch, "E288", {"start": v(-109.74, 119.18) * mm, "end": v(-109.93, 118.73) * mm});
            skLineSegment(sketch, "E289", {"start": v(-109.93, 118.73) * mm, "end": v(-110.15, 118.28) * mm});
            skLineSegment(sketch, "E290", {"start": v(-110.15, 118.28) * mm, "end": v(-110.38, 117.85) * mm});
            skLineSegment(sketch, "E291", {"start": v(-110.38, 117.85) * mm, "end": v(-110.64, 117.43) * mm});
            skLineSegment(sketch, "E292", {"start": v(-110.64, 117.43) * mm, "end": v(-110.93, 117.02) * mm});
            skLineSegment(sketch, "E293", {"start": v(-110.93, 117.02) * mm, "end": v(-111.23, 116.62) * mm});
            skLineSegment(sketch, "E294", {"start": v(-111.23, 116.62) * mm, "end": v(-111.55, 116.24) * mm});
            skLineSegment(sketch, "E295", {"start": v(-111.55, 116.24) * mm, "end": v(-111.9, 115.88) * mm});
            skLineSegment(sketch, "E296", {"start": v(-111.9, 115.88) * mm, "end": v(-112.26, 115.53) * mm});
            skLineSegment(sketch, "E297", {"start": v(-112.26, 115.53) * mm, "end": v(-112.63, 115.2) * mm});
            skLineSegment(sketch, "E298", {"start": v(-112.63, 115.2) * mm, "end": v(-113.02, 114.9) * mm});
            skLineSegment(sketch, "E299", {"start": v(-113.02, 114.9) * mm, "end": v(-113.43, 114.62) * mm});
            skLineSegment(sketch, "E300", {"start": v(-113.43, 114.62) * mm, "end": v(-113.84, 114.36) * mm});
            skLineSegment(sketch, "E301", {"start": v(-113.84, 114.36) * mm, "end": v(-114.27, 114.12) * mm});
            skLineSegment(sketch, "E302", {"start": v(-114.27, 114.12) * mm, "end": v(-114.71, 113.9) * mm});
            skLineSegment(sketch, "E303", {"start": v(-114.71, 113.9) * mm, "end": v(-115.16, 113.7) * mm});
            skLineSegment(sketch, "E304", {"start": v(-115.16, 113.7) * mm, "end": v(-115.62, 113.53) * mm});
            skLineSegment(sketch, "E305", {"start": v(-115.62, 113.53) * mm, "end": v(-116.1, 113.38) * mm});
            skLineSegment(sketch, "E306", {"start": v(-116.1, 113.38) * mm, "end": v(-116.57, 113.25) * mm});
            skLineSegment(sketch, "E307", {"start": v(-116.57, 113.25) * mm, "end": v(-117.05, 113.15) * mm});
            skLineSegment(sketch, "E308", {"start": v(-117.05, 113.15) * mm, "end": v(-117.53, 113.07) * mm});
            skLineSegment(sketch, "E309", {"start": v(-117.53, 113.07) * mm, "end": v(-118.03, 113.01) * mm});
            skLineSegment(sketch, "E310", {"start": v(-118.03, 113.01) * mm, "end": v(-118.52, 112.98) * mm});
            skLineSegment(sketch, "E311", {"start": v(-118.52, 112.98) * mm, "end": v(-119.02, 112.98) * mm});
            skLineSegment(sketch, "E312", {"start": v(-119.02, 112.98) * mm, "end": v(-136.58, 112.98) * mm});
            skLineSegment(sketch, "E313", {"start": v(-119.02, 112.98) * mm, "end": v(-118.6, 112.98) * mm});
            skLineSegment(sketch, "E314", {"start": v(-118.6, 112.98) * mm, "end": v(-118.2, 112.95) * mm});
            skLineSegment(sketch, "E315", {"start": v(-118.2, 112.95) * mm, "end": v(-117.8, 112.9) * mm});
            skLineSegment(sketch, "E316", {"start": v(-117.8, 112.9) * mm, "end": v(-117.4, 112.85) * mm});
            skLineSegment(sketch, "E317", {"start": v(-117.4, 112.85) * mm, "end": v(-117, 112.76) * mm});
            skLineSegment(sketch, "E318", {"start": v(-117, 112.76) * mm, "end": v(-116.61, 112.66) * mm});
            skLineSegment(sketch, "E319", {"start": v(-116.61, 112.66) * mm, "end": v(-116.23, 112.53) * mm});
            skLineSegment(sketch, "E320", {"start": v(-116.23, 112.53) * mm, "end": v(-115.85, 112.4) * mm});
            skLineSegment(sketch, "E321", {"start": v(-115.85, 112.4) * mm, "end": v(-115.48, 112.23) * mm});
            skLineSegment(sketch, "E322", {"start": v(-115.48, 112.23) * mm, "end": v(-115.12, 112.05) * mm});
            skLineSegment(sketch, "E323", {"start": v(-115.12, 112.05) * mm, "end": v(-114.76, 111.85) * mm});
            skLineSegment(sketch, "E324", {"start": v(-114.76, 111.85) * mm, "end": v(-114.42, 111.63) * mm});
            skLineSegment(sketch, "E325", {"start": v(-114.42, 111.63) * mm, "end": v(-114.1, 111.4) * mm});
            skLineSegment(sketch, "E326", {"start": v(-114.1, 111.4) * mm, "end": v(-113.77, 111.15) * mm});
            skLineSegment(sketch, "E327", {"start": v(-113.77, 111.15) * mm, "end": v(-113.46, 110.88) * mm});
            skLineSegment(sketch, "E328", {"start": v(-113.46, 110.88) * mm, "end": v(-113.17, 110.6) * mm});
            skLineSegment(sketch, "E329", {"start": v(-113.17, 110.6) * mm, "end": v(-112.83, 110.1) * mm});
            skLineSegment(sketch, "E330", {"start": v(-112.83, 110.1) * mm, "end": v(-112.51, 109.58) * mm});
            skLineSegment(sketch, "E331", {"start": v(-112.51, 109.58) * mm, "end": v(-112.22, 109.06) * mm});
            skLineSegment(sketch, "E332", {"start": v(-112.22, 109.06) * mm, "end": v(-111.95, 108.52) * mm});
            skLineSegment(sketch, "E333", {"start": v(-111.95, 108.52) * mm, "end": v(-111.7, 107.97) * mm});
            skLineSegment(sketch, "E334", {"start": v(-111.7, 107.97) * mm, "end": v(-111.48, 107.41) * mm});
            skLineSegment(sketch, "E335", {"start": v(-111.48, 107.41) * mm, "end": v(-111.29, 106.85) * mm});
            skLineSegment(sketch, "E336", {"start": v(-111.29, 106.85) * mm, "end": v(-111.12, 106.27) * mm});
            skLineSegment(sketch, "E337", {"start": v(-111.12, 106.27) * mm, "end": v(-110.98, 105.7) * mm});
            skLineSegment(sketch, "E338", {"start": v(-110.98, 105.7) * mm, "end": v(-110.86, 105.1) * mm});
            skLineSegment(sketch, "E339", {"start": v(-110.86, 105.1) * mm, "end": v(-110.77, 104.51) * mm});
            skLineSegment(sketch, "E340", {"start": v(-110.77, 104.51) * mm, "end": v(-110.7, 103.92) * mm});
            skLineSegment(sketch, "E341", {"start": v(-110.7, 103.92) * mm, "end": v(-110.66, 103.32) * mm});
            skLineSegment(sketch, "E342", {"start": v(-110.66, 103.32) * mm, "end": v(-110.65, 102.72) * mm});
            skLineSegment(sketch, "E343", {"start": v(-110.65, 102.72) * mm, "end": v(-110.67, 102.11) * mm});
            skLineSegment(sketch, "E344", {"start": v(-110.67, 102.11) * mm, "end": v(-110.7, 101.5) * mm});
            skLineSegment(sketch, "E345", {"start": v(-110.7, 101.5) * mm, "end": v(-110.72, 100.97) * mm});
            skLineSegment(sketch, "E346", {"start": v(-110.72, 100.97) * mm, "end": v(-110.71, 100.43) * mm});
            skLineSegment(sketch, "E347", {"start": v(-110.71, 100.43) * mm, "end": v(-110.7, 99.9) * mm});
            skLineSegment(sketch, "E348", {"start": v(-110.7, 99.9) * mm, "end": v(-110.68, 99.36) * mm});
            skLineSegment(sketch, "E349", {"start": v(-110.68, 99.36) * mm, "end": v(-110.65, 98.82) * mm});
            skLineSegment(sketch, "E350", {"start": v(-110.65, 98.82) * mm, "end": v(-110.6, 98.28) * mm});
            skLineSegment(sketch, "E351", {"start": v(-110.6, 98.28) * mm, "end": v(-110.56, 97.75) * mm});
            skLineSegment(sketch, "E352", {"start": v(-110.56, 97.75) * mm, "end": v(-110.5, 97.21) * mm});
            skLineSegment(sketch, "E353", {"start": v(-110.5, 97.21) * mm, "end": v(-110.43, 96.68) * mm});
            skLineSegment(sketch, "E354", {"start": v(-110.43, 96.68) * mm, "end": v(-110.35, 96.14) * mm});
            skLineSegment(sketch, "E355", {"start": v(-110.35, 96.14) * mm, "end": v(-110.26, 95.61) * mm});
            skLineSegment(sketch, "E356", {"start": v(-110.26, 95.61) * mm, "end": v(-110.16, 95.08) * mm});
            skLineSegment(sketch, "E357", {"start": v(-110.16, 95.08) * mm, "end": v(-110.06, 94.56) * mm});
            skLineSegment(sketch, "E358", {"start": v(-110.06, 94.56) * mm, "end": v(-109.94, 94.03) * mm});
            skLineSegment(sketch, "E359", {"start": v(-109.94, 94.03) * mm, "end": v(-109.81, 93.5) * mm});
            skLineSegment(sketch, "E360", {"start": v(-109.81, 93.5) * mm, "end": v(-109.68, 92.99) * mm});
            skLineSegment(sketch, "E361", {"start": v(-83.77, 92.43) * mm, "end": v(-84.2, 92.43) * mm});
            skLineSegment(sketch, "E362", {"start": v(-84.2, 92.43) * mm, "end": v(-84.61, 92.43) * mm});
            skLineSegment(sketch, "E363", {"start": v(-84.61, 92.43) * mm, "end": v(-85.03, 92.45) * mm});
            skLineSegment(sketch, "E364", {"start": v(-85.03, 92.45) * mm, "end": v(-85.44, 92.48) * mm});
            skLineSegment(sketch, "E365", {"start": v(-85.44, 92.48) * mm, "end": v(-85.86, 92.52) * mm});
            skLineSegment(sketch, "E366", {"start": v(-85.86, 92.52) * mm, "end": v(-86.27, 92.57) * mm});
            skLineSegment(sketch, "E367", {"start": v(-86.27, 92.57) * mm, "end": v(-86.69, 92.63) * mm});
            skLineSegment(sketch, "E368", {"start": v(-86.69, 92.63) * mm, "end": v(-87.1, 92.7) * mm});
            skLineSegment(sketch, "E369", {"start": v(-87.1, 92.7) * mm, "end": v(-87.5, 92.77) * mm});
            skLineSegment(sketch, "E370", {"start": v(-87.5, 92.77) * mm, "end": v(-87.9, 92.86) * mm});
            skLineSegment(sketch, "E371", {"start": v(-87.9, 92.86) * mm, "end": v(-88.3, 92.96) * mm});
            skLineSegment(sketch, "E372", {"start": v(-88.3, 92.96) * mm, "end": v(-88.7, 93.07) * mm});
            skLineSegment(sketch, "E373", {"start": v(-88.7, 93.07) * mm, "end": v(-89.1, 93.2) * mm});
            skLineSegment(sketch, "E374", {"start": v(-89.1, 93.2) * mm, "end": v(-89.5, 93.32) * mm});
            skLineSegment(sketch, "E375", {"start": v(-89.5, 93.32) * mm, "end": v(-89.89, 93.46) * mm});
            skLineSegment(sketch, "E376", {"start": v(-89.89, 93.46) * mm, "end": v(-90.27, 93.6) * mm});
            skLineSegment(sketch, "E377", {"start": v(-90.27, 93.6) * mm, "end": v(-90.66, 93.77) * mm});
            skLineSegment(sketch, "E378", {"start": v(-90.66, 93.77) * mm, "end": v(-91.03, 93.93) * mm});
            skLineSegment(sketch, "E379", {"start": v(-91.03, 93.93) * mm, "end": v(-91.4, 94.11) * mm});
            skLineSegment(sketch, "E380", {"start": v(-91.4, 94.11) * mm, "end": v(-91.78, 94.3) * mm});
            skLineSegment(sketch, "E381", {"start": v(-91.78, 94.3) * mm, "end": v(-92.14, 94.5) * mm});
            skLineSegment(sketch, "E382", {"start": v(-92.14, 94.5) * mm, "end": v(-92.5, 94.7) * mm});
            skLineSegment(sketch, "E383", {"start": v(-92.5, 94.7) * mm, "end": v(-92.86, 94.9) * mm});
            skLineSegment(sketch, "E384", {"start": v(-92.86, 94.9) * mm, "end": v(-93.21, 95.13) * mm});
            skLineSegment(sketch, "E385", {"start": v(-93.21, 95.13) * mm, "end": v(-93.56, 95.36) * mm});
            skLineSegment(sketch, "E386", {"start": v(-93.56, 95.36) * mm, "end": v(-93.9, 95.6) * mm});
            skLineSegment(sketch, "E387", {"start": v(-93.9, 95.6) * mm, "end": v(-94.23, 95.85) * mm});
            skLineSegment(sketch, "E388", {"start": v(-94.23, 95.85) * mm, "end": v(-94.56, 96.1) * mm});
            skLineSegment(sketch, "E389", {"start": v(-94.56, 96.1) * mm, "end": v(-94.88, 96.37) * mm});
            skLineSegment(sketch, "E390", {"start": v(-94.88, 96.37) * mm, "end": v(-95.2, 96.65) * mm});
            skLineSegment(sketch, "E391", {"start": v(-95.2, 96.65) * mm, "end": v(-95.5, 96.93) * mm});
            skLineSegment(sketch, "E392", {"start": v(-95.5, 96.93) * mm, "end": v(-95.8, 97.22) * mm});
            skLineSegment(sketch, "E393", {"start": v(-95.8, 97.22) * mm, "end": v(-96.16, 97.6) * mm});
            skLineSegment(sketch, "E394", {"start": v(-96.16, 97.6) * mm, "end": v(-96.5, 98) * mm});
            skLineSegment(sketch, "E395", {"start": v(-96.5, 98) * mm, "end": v(-96.82, 98.39) * mm});
            skLineSegment(sketch, "E396", {"start": v(-96.82, 98.39) * mm, "end": v(-97.14, 98.8) * mm});
            skLineSegment(sketch, "E397", {"start": v(-97.14, 98.8) * mm, "end": v(-97.45, 99.2) * mm});
            skLineSegment(sketch, "E398", {"start": v(-97.45, 99.2) * mm, "end": v(-97.75, 99.62) * mm});
            skLineSegment(sketch, "E399", {"start": v(-97.75, 99.62) * mm, "end": v(-98.04, 100.04) * mm});
            skLineSegment(sketch, "E400", {"start": v(-98.04, 100.04) * mm, "end": v(-98.31, 100.47) * mm});
            skLineSegment(sketch, "E401", {"start": v(-98.31, 100.47) * mm, "end": v(-98.58, 100.91) * mm});
            skLineSegment(sketch, "E402", {"start": v(-98.58, 100.91) * mm, "end": v(-98.83, 101.35) * mm});
            skLineSegment(sketch, "E403", {"start": v(-98.83, 101.35) * mm, "end": v(-99.07, 101.8) * mm});
            skLineSegment(sketch, "E404", {"start": v(-99.07, 101.8) * mm, "end": v(-99.3, 102.26) * mm});
            skLineSegment(sketch, "E405", {"start": v(-99.3, 102.26) * mm, "end": v(-99.52, 102.72) * mm});
            skLineSegment(sketch, "E406", {"start": v(-99.52, 102.72) * mm, "end": v(-99.73, 103.18) * mm});
            skLineSegment(sketch, "E407", {"start": v(-99.73, 103.18) * mm, "end": v(-99.93, 103.65) * mm});
            skLineSegment(sketch, "E408", {"start": v(-99.93, 103.65) * mm, "end": v(-100.11, 104.13) * mm});
            skLineSegment(sketch, "E409", {"start": v(-100.11, 104.13) * mm, "end": v(-100.29, 104.6) * mm});
            skLineSegment(sketch, "E410", {"start": v(-100.29, 104.6) * mm, "end": v(-100.45, 105.09) * mm});
            skLineSegment(sketch, "E411", {"start": v(-100.45, 105.09) * mm, "end": v(-100.6, 105.57) * mm});
            skLineSegment(sketch, "E412", {"start": v(-100.6, 105.57) * mm, "end": v(-100.74, 106.06) * mm});
            skLineSegment(sketch, "E413", {"start": v(-100.74, 106.06) * mm, "end": v(-100.86, 106.56) * mm});
            skLineSegment(sketch, "E414", {"start": v(-100.86, 106.56) * mm, "end": v(-100.98, 107.06) * mm});
            skLineSegment(sketch, "E415", {"start": v(-100.98, 107.06) * mm, "end": v(-101.08, 107.56) * mm});
            skLineSegment(sketch, "E416", {"start": v(-101.08, 107.56) * mm, "end": v(-101.17, 108.06) * mm});
            skLineSegment(sketch, "E417", {"start": v(-101.17, 108.06) * mm, "end": v(-101.25, 108.56) * mm});
            skLineSegment(sketch, "E418", {"start": v(-101.25, 108.56) * mm, "end": v(-101.31, 109.07) * mm});
            skLineSegment(sketch, "E419", {"start": v(-101.31, 109.07) * mm, "end": v(-101.36, 109.58) * mm});
            skLineSegment(sketch, "E420", {"start": v(-101.36, 109.58) * mm, "end": v(-101.4, 110.1) * mm});
            skLineSegment(sketch, "E421", {"start": v(-101.4, 110.1) * mm, "end": v(-101.43, 110.6) * mm});
            skLineSegment(sketch, "E422", {"start": v(-101.43, 110.6) * mm, "end": v(-101.44, 111.12) * mm});
            skLineSegment(sketch, "E423", {"start": v(-101.44, 111.12) * mm, "end": v(-101.44, 111.64) * mm});
            skLineSegment(sketch, "E424", {"start": v(-101.44, 111.64) * mm, "end": v(-101.43, 112.15) * mm});
            skLineSegment(sketch, "E425", {"start": v(-101.43, 112.15) * mm, "end": v(-101.45, 112.71) * mm});
            skLineSegment(sketch, "E426", {"start": v(-101.45, 112.71) * mm, "end": v(-101.45, 113.28) * mm});
            skLineSegment(sketch, "E427", {"start": v(-101.45, 113.28) * mm, "end": v(-101.44, 113.83) * mm});
            skLineSegment(sketch, "E428", {"start": v(-101.44, 113.83) * mm, "end": v(-101.41, 114.4) * mm});
            skLineSegment(sketch, "E429", {"start": v(-101.41, 114.4) * mm, "end": v(-101.37, 114.95) * mm});
            skLineSegment(sketch, "E430", {"start": v(-101.37, 114.95) * mm, "end": v(-101.32, 115.5) * mm});
            skLineSegment(sketch, "E431", {"start": v(-101.32, 115.5) * mm, "end": v(-101.25, 116.05) * mm});
            skLineSegment(sketch, "E432", {"start": v(-101.25, 116.05) * mm, "end": v(-101.17, 116.6) * mm});
            skLineSegment(sketch, "E433", {"start": v(-101.17, 116.6) * mm, "end": v(-101.07, 117.15) * mm});
            skLineSegment(sketch, "E434", {"start": v(-101.07, 117.15) * mm, "end": v(-100.96, 117.7) * mm});
            skLineSegment(sketch, "E435", {"start": v(-100.96, 117.7) * mm, "end": v(-100.84, 118.23) * mm});
            skLineSegment(sketch, "E436", {"start": v(-100.84, 118.23) * mm, "end": v(-100.7, 118.77) * mm});
            skLineSegment(sketch, "E437", {"start": v(-100.7, 118.77) * mm, "end": v(-100.55, 119.3) * mm});
            skLineSegment(sketch, "E438", {"start": v(-100.55, 119.3) * mm, "end": v(-100.4, 119.83) * mm});
            skLineSegment(sketch, "E439", {"start": v(-100.4, 119.83) * mm, "end": v(-100.22, 120.35) * mm});
            skLineSegment(sketch, "E440", {"start": v(-100.22, 120.35) * mm, "end": v(-100.03, 120.87) * mm});
            skLineSegment(sketch, "E441", {"start": v(-100.03, 120.87) * mm, "end": v(-99.83, 121.39) * mm});
            skLineSegment(sketch, "E442", {"start": v(-99.83, 121.39) * mm, "end": v(-99.62, 121.9) * mm});
            skLineSegment(sketch, "E443", {"start": v(-99.62, 121.9) * mm, "end": v(-99.39, 122.4) * mm});
            skLineSegment(sketch, "E444", {"start": v(-99.39, 122.4) * mm, "end": v(-99.15, 122.9) * mm});
            skLineSegment(sketch, "E445", {"start": v(-99.15, 122.9) * mm, "end": v(-98.9, 123.4) * mm});
            skLineSegment(sketch, "E446", {"start": v(-98.9, 123.4) * mm, "end": v(-98.64, 123.88) * mm});
            skLineSegment(sketch, "E447", {"start": v(-98.64, 123.88) * mm, "end": v(-98.36, 124.36) * mm});
            skLineSegment(sketch, "E448", {"start": v(-98.36, 124.36) * mm, "end": v(-98.07, 124.84) * mm});
            skLineSegment(sketch, "E449", {"start": v(-98.07, 124.84) * mm, "end": v(-97.77, 125.3) * mm});
            skLineSegment(sketch, "E450", {"start": v(-97.77, 125.3) * mm, "end": v(-97.46, 125.77) * mm});
            skLineSegment(sketch, "E451", {"start": v(-97.46, 125.77) * mm, "end": v(-97.14, 126.22) * mm});
            skLineSegment(sketch, "E452", {"start": v(-97.14, 126.22) * mm, "end": v(-96.8, 126.66) * mm});
            skLineSegment(sketch, "E453", {"start": v(-96.8, 126.66) * mm, "end": v(-96.45, 127.1) * mm});
            skLineSegment(sketch, "E454", {"start": v(-96.45, 127.1) * mm, "end": v(-96.1, 127.53) * mm});
            skLineSegment(sketch, "E455", {"start": v(-96.1, 127.53) * mm, "end": v(-95.72, 127.95) * mm});
            skLineSegment(sketch, "E456", {"start": v(-95.72, 127.95) * mm, "end": v(-95.34, 128.36) * mm});
            skLineSegment(sketch, "E457", {"start": v(-95.34, 128.36) * mm, "end": v(-95.06, 128.65) * mm});
            skLineSegment(sketch, "E458", {"start": v(-95.06, 128.65) * mm, "end": v(-94.76, 128.93) * mm});
            skLineSegment(sketch, "E459", {"start": v(-94.76, 128.93) * mm, "end": v(-94.46, 129.2) * mm});
            skLineSegment(sketch, "E460", {"start": v(-94.46, 129.2) * mm, "end": v(-94.16, 129.47) * mm});
            skLineSegment(sketch, "E461", {"start": v(-94.16, 129.47) * mm, "end": v(-93.85, 129.73) * mm});
            skLineSegment(sketch, "E462", {"start": v(-93.85, 129.73) * mm, "end": v(-93.53, 129.98) * mm});
            skLineSegment(sketch, "E463", {"start": v(-93.53, 129.98) * mm, "end": v(-93.2, 130.22) * mm});
            skLineSegment(sketch, "E464", {"start": v(-93.2, 130.22) * mm, "end": v(-92.87, 130.45) * mm});
            skLineSegment(sketch, "E465", {"start": v(-92.87, 130.45) * mm, "end": v(-92.54, 130.68) * mm});
            skLineSegment(sketch, "E466", {"start": v(-92.54, 130.68) * mm, "end": v(-92.2, 130.89) * mm});
            skLineSegment(sketch, "E467", {"start": v(-92.2, 130.89) * mm, "end": v(-91.85, 131.1) * mm});
            skLineSegment(sketch, "E468", {"start": v(-91.85, 131.1) * mm, "end": v(-91.5, 131.3) * mm});
            skLineSegment(sketch, "E469", {"start": v(-91.5, 131.3) * mm, "end": v(-91.15, 131.48) * mm});
            skLineSegment(sketch, "E470", {"start": v(-91.15, 131.48) * mm, "end": v(-90.79, 131.65) * mm});
            skLineSegment(sketch, "E471", {"start": v(-90.79, 131.65) * mm, "end": v(-90.42, 131.82) * mm});
            skLineSegment(sketch, "E472", {"start": v(-90.42, 131.82) * mm, "end": v(-90.06, 131.98) * mm});
            skLineSegment(sketch, "E473", {"start": v(-90.06, 131.98) * mm, "end": v(-89.68, 132.13) * mm});
            skLineSegment(sketch, "E474", {"start": v(-89.68, 132.13) * mm, "end": v(-89.3, 132.27) * mm});
            skLineSegment(sketch, "E475", {"start": v(-89.3, 132.27) * mm, "end": v(-88.93, 132.4) * mm});
            skLineSegment(sketch, "E476", {"start": v(-88.93, 132.4) * mm, "end": v(-88.55, 132.52) * mm});
            skLineSegment(sketch, "E477", {"start": v(-88.55, 132.52) * mm, "end": v(-88.16, 132.63) * mm});
            skLineSegment(sketch, "E478", {"start": v(-88.16, 132.63) * mm, "end": v(-87.77, 132.74) * mm});
            skLineSegment(sketch, "E479", {"start": v(-87.77, 132.74) * mm, "end": v(-87.38, 132.83) * mm});
            skLineSegment(sketch, "E480", {"start": v(-87.38, 132.83) * mm, "end": v(-86.99, 132.9) * mm});
            skLineSegment(sketch, "E481", {"start": v(-86.99, 132.9) * mm, "end": v(-86.59, 132.98) * mm});
            skLineSegment(sketch, "E482", {"start": v(-86.59, 132.98) * mm, "end": v(-86.2, 133.04) * mm});
            skLineSegment(sketch, "E483", {"start": v(-86.2, 133.04) * mm, "end": v(-85.79, 133.1) * mm});
            skLineSegment(sketch, "E484", {"start": v(-85.79, 133.1) * mm, "end": v(-85.39, 133.13) * mm});
            skLineSegment(sketch, "E485", {"start": v(-85.39, 133.13) * mm, "end": v(-84.98, 133.16) * mm});
            skLineSegment(sketch, "E486", {"start": v(-84.98, 133.16) * mm, "end": v(-84.58, 133.18) * mm});
            skLineSegment(sketch, "E487", {"start": v(-84.58, 133.18) * mm, "end": v(-84.17, 133.2) * mm});
            skLineSegment(sketch, "E488", {"start": v(-84.17, 133.2) * mm, "end": v(-83.76, 133.19) * mm});
            skLineSegment(sketch, "E489", {"start": v(-83.76, 133.19) * mm, "end": v(-83.35, 133.18) * mm});
            skLineSegment(sketch, "E490", {"start": v(-83.35, 133.18) * mm, "end": v(-82.94, 133.17) * mm});
            skLineSegment(sketch, "E491", {"start": v(-82.94, 133.17) * mm, "end": v(-82.52, 133.15) * mm});
            skLineSegment(sketch, "E492", {"start": v(-82.52, 133.15) * mm, "end": v(-82.11, 133.1) * mm});
            skLineSegment(sketch, "E493", {"start": v(-82.11, 133.1) * mm, "end": v(-81.7, 133.06) * mm});
            skLineSegment(sketch, "E494", {"start": v(-81.7, 133.06) * mm, "end": v(-81.3, 133) * mm});
            skLineSegment(sketch, "E495", {"start": v(-81.3, 133) * mm, "end": v(-80.9, 132.94) * mm});
            skLineSegment(sketch, "E496", {"start": v(-80.9, 132.94) * mm, "end": v(-80.5, 132.86) * mm});
            skLineSegment(sketch, "E497", {"start": v(-80.5, 132.86) * mm, "end": v(-80.1, 132.77) * mm});
            skLineSegment(sketch, "E498", {"start": v(-80.1, 132.77) * mm, "end": v(-79.7, 132.68) * mm});
            skLineSegment(sketch, "E499", {"start": v(-79.7, 132.68) * mm, "end": v(-79.3, 132.57) * mm});
            skLineSegment(sketch, "E500", {"start": v(-79.3, 132.57) * mm, "end": v(-78.91, 132.45) * mm});
            skLineSegment(sketch, "E501", {"start": v(-78.91, 132.45) * mm, "end": v(-78.52, 132.32) * mm});
            skLineSegment(sketch, "E502", {"start": v(-78.52, 132.32) * mm, "end": v(-78.14, 132.19) * mm});
            skLineSegment(sketch, "E503", {"start": v(-78.14, 132.19) * mm, "end": v(-77.76, 132.04) * mm});
            skLineSegment(sketch, "E504", {"start": v(-77.76, 132.04) * mm, "end": v(-77.38, 131.88) * mm});
            skLineSegment(sketch, "E505", {"start": v(-77.38, 131.88) * mm, "end": v(-77.01, 131.72) * mm});
            skLineSegment(sketch, "E506", {"start": v(-77.01, 131.72) * mm, "end": v(-76.64, 131.54) * mm});
            skLineSegment(sketch, "E507", {"start": v(-76.64, 131.54) * mm, "end": v(-76.28, 131.36) * mm});
            skLineSegment(sketch, "E508", {"start": v(-76.28, 131.36) * mm, "end": v(-75.92, 131.16) * mm});
            skLineSegment(sketch, "E509", {"start": v(-75.92, 131.16) * mm, "end": v(-75.57, 130.96) * mm});
            skLineSegment(sketch, "E510", {"start": v(-75.57, 130.96) * mm, "end": v(-75.22, 130.75) * mm});
            skLineSegment(sketch, "E511", {"start": v(-75.22, 130.75) * mm, "end": v(-74.87, 130.52) * mm});
            skLineSegment(sketch, "E512", {"start": v(-74.87, 130.52) * mm, "end": v(-74.54, 130.3) * mm});
            skLineSegment(sketch, "E513", {"start": v(-74.54, 130.3) * mm, "end": v(-74.2, 130.05) * mm});
            skLineSegment(sketch, "E514", {"start": v(-74.2, 130.05) * mm, "end": v(-73.88, 129.8) * mm});
            skLineSegment(sketch, "E515", {"start": v(-73.88, 129.8) * mm, "end": v(-73.56, 129.55) * mm});
            skLineSegment(sketch, "E516", {"start": v(-73.56, 129.55) * mm, "end": v(-73.24, 129.28) * mm});
            skLineSegment(sketch, "E517", {"start": v(-73.24, 129.28) * mm, "end": v(-72.94, 129) * mm});
            skLineSegment(sketch, "E518", {"start": v(-72.94, 129) * mm, "end": v(-72.64, 128.73) * mm});
            skLineSegment(sketch, "E519", {"start": v(-72.64, 128.73) * mm, "end": v(-72.34, 128.44) * mm});
            skLineSegment(sketch, "E520", {"start": v(-72.34, 128.44) * mm, "end": v(-72.05, 128.14) * mm});
            skLineSegment(sketch, "E521", {"start": v(-72.05, 128.14) * mm, "end": v(-71.68, 127.73) * mm});
            skLineSegment(sketch, "E522", {"start": v(-71.68, 127.73) * mm, "end": v(-71.33, 127.31) * mm});
            skLineSegment(sketch, "E523", {"start": v(-71.33, 127.31) * mm, "end": v(-70.98, 126.88) * mm});
            skLineSegment(sketch, "E524", {"start": v(-70.98, 126.88) * mm, "end": v(-70.64, 126.45) * mm});
            skLineSegment(sketch, "E525", {"start": v(-70.64, 126.45) * mm, "end": v(-70.32, 126) * mm});
            skLineSegment(sketch, "E526", {"start": v(-70.32, 126) * mm, "end": v(-70, 125.56) * mm});
            skLineSegment(sketch, "E527", {"start": v(-70, 125.56) * mm, "end": v(-69.7, 125.1) * mm});
            skLineSegment(sketch, "E528", {"start": v(-69.7, 125.1) * mm, "end": v(-69.41, 124.64) * mm});
            skLineSegment(sketch, "E529", {"start": v(-69.41, 124.64) * mm, "end": v(-69.13, 124.17) * mm});
            skLineSegment(sketch, "E530", {"start": v(-69.13, 124.17) * mm, "end": v(-68.87, 123.7) * mm});
            skLineSegment(sketch, "E531", {"start": v(-68.87, 123.7) * mm, "end": v(-68.61, 123.21) * mm});
            skLineSegment(sketch, "E532", {"start": v(-68.61, 123.21) * mm, "end": v(-68.37, 122.73) * mm});
            skLineSegment(sketch, "E533", {"start": v(-68.37, 122.73) * mm, "end": v(-68.14, 122.23) * mm});
            skLineSegment(sketch, "E534", {"start": v(-68.14, 122.23) * mm, "end": v(-67.92, 121.73) * mm});
            skLineSegment(sketch, "E535", {"start": v(-67.92, 121.73) * mm, "end": v(-67.72, 121.23) * mm});
            skLineSegment(sketch, "E536", {"start": v(-67.72, 121.23) * mm, "end": v(-67.53, 120.72) * mm});
            skLineSegment(sketch, "E537", {"start": v(-67.53, 120.72) * mm, "end": v(-67.35, 120.2) * mm});
            skLineSegment(sketch, "E538", {"start": v(-67.35, 120.2) * mm, "end": v(-67.18, 119.69) * mm});
            skLineSegment(sketch, "E539", {"start": v(-67.18, 119.69) * mm, "end": v(-67.03, 119.17) * mm});
            skLineSegment(sketch, "E540", {"start": v(-67.03, 119.17) * mm, "end": v(-66.88, 118.64) * mm});
            skLineSegment(sketch, "E541", {"start": v(-66.88, 118.64) * mm, "end": v(-66.75, 118.11) * mm});
            skLineSegment(sketch, "E542", {"start": v(-66.75, 118.11) * mm, "end": v(-66.64, 117.58) * mm});
            skLineSegment(sketch, "E543", {"start": v(-66.64, 117.58) * mm, "end": v(-66.54, 117.05) * mm});
            skLineSegment(sketch, "E544", {"start": v(-66.54, 117.05) * mm, "end": v(-66.45, 116.5) * mm});
            skLineSegment(sketch, "E545", {"start": v(-66.45, 116.5) * mm, "end": v(-66.37, 115.97) * mm});
            skLineSegment(sketch, "E546", {"start": v(-66.37, 115.97) * mm, "end": v(-66.3, 115.42) * mm});
            skLineSegment(sketch, "E547", {"start": v(-66.3, 115.42) * mm, "end": v(-66.26, 114.88) * mm});
            skLineSegment(sketch, "E548", {"start": v(-66.26, 114.88) * mm, "end": v(-66.22, 114.33) * mm});
            skLineSegment(sketch, "E549", {"start": v(-66.22, 114.33) * mm, "end": v(-66.2, 113.78) * mm});
            skLineSegment(sketch, "E550", {"start": v(-66.2, 113.78) * mm, "end": v(-66.2, 113.23) * mm});
            skLineSegment(sketch, "E551", {"start": v(-66.2, 113.23) * mm, "end": v(-66.2, 112.68) * mm});
            skLineSegment(sketch, "E552", {"start": v(-66.2, 112.68) * mm, "end": v(-66.22, 112.13) * mm});
            skLineSegment(sketch, "E553", {"start": v(-66.22, 112.13) * mm, "end": v(-66.21, 111.61) * mm});
            skLineSegment(sketch, "E554", {"start": v(-66.21, 111.61) * mm, "end": v(-66.22, 111.1) * mm});
            skLineSegment(sketch, "E555", {"start": v(-66.22, 111.1) * mm, "end": v(-66.23, 110.59) * mm});
            skLineSegment(sketch, "E556", {"start": v(-66.23, 110.59) * mm, "end": v(-66.26, 110.08) * mm});
            skLineSegment(sketch, "E557", {"start": v(-66.26, 110.08) * mm, "end": v(-66.3, 109.57) * mm});
            skLineSegment(sketch, "E558", {"start": v(-66.3, 109.57) * mm, "end": v(-66.36, 109.06) * mm});
            skLineSegment(sketch, "E559", {"start": v(-66.36, 109.06) * mm, "end": v(-66.43, 108.56) * mm});
            skLineSegment(sketch, "E560", {"start": v(-66.43, 108.56) * mm, "end": v(-66.51, 108.05) * mm});
            skLineSegment(sketch, "E561", {"start": v(-66.51, 108.05) * mm, "end": v(-66.6, 107.55) * mm});
            skLineSegment(sketch, "E562", {"start": v(-66.6, 107.55) * mm, "end": v(-66.71, 107.06) * mm});
            skLineSegment(sketch, "E563", {"start": v(-66.71, 107.06) * mm, "end": v(-66.83, 106.56) * mm});
            skLineSegment(sketch, "E564", {"start": v(-66.83, 106.56) * mm, "end": v(-66.96, 106.07) * mm});
            skLineSegment(sketch, "E565", {"start": v(-66.96, 106.07) * mm, "end": v(-67.1, 105.58) * mm});
            skLineSegment(sketch, "E566", {"start": v(-67.1, 105.58) * mm, "end": v(-67.26, 105.1) * mm});
            skLineSegment(sketch, "E567", {"start": v(-67.26, 105.1) * mm, "end": v(-67.42, 104.62) * mm});
            skLineSegment(sketch, "E568", {"start": v(-67.42, 104.62) * mm, "end": v(-67.6, 104.15) * mm});
            skLineSegment(sketch, "E569", {"start": v(-67.6, 104.15) * mm, "end": v(-67.8, 103.68) * mm});
            skLineSegment(sketch, "E570", {"start": v(-67.8, 103.68) * mm, "end": v(-68, 103.2) * mm});
            skLineSegment(sketch, "E571", {"start": v(-68, 103.2) * mm, "end": v(-68.2, 102.75) * mm});
            skLineSegment(sketch, "E572", {"start": v(-68.2, 102.75) * mm, "end": v(-68.43, 102.3) * mm});
            skLineSegment(sketch, "E573", {"start": v(-68.43, 102.3) * mm, "end": v(-68.67, 101.84) * mm});
            skLineSegment(sketch, "E574", {"start": v(-68.67, 101.84) * mm, "end": v(-68.91, 101.4) * mm});
            skLineSegment(sketch, "E575", {"start": v(-68.91, 101.4) * mm, "end": v(-69.17, 100.96) * mm});
            skLineSegment(sketch, "E576", {"start": v(-69.17, 100.96) * mm, "end": v(-69.44, 100.53) * mm});
            skLineSegment(sketch, "E577", {"start": v(-69.44, 100.53) * mm, "end": v(-69.72, 100.1) * mm});
            skLineSegment(sketch, "E578", {"start": v(-69.72, 100.1) * mm, "end": v(-70.01, 99.69) * mm});
            skLineSegment(sketch, "E579", {"start": v(-70.01, 99.69) * mm, "end": v(-70.31, 99.27) * mm});
            skLineSegment(sketch, "E580", {"start": v(-70.31, 99.27) * mm, "end": v(-70.63, 98.87) * mm});
            skLineSegment(sketch, "E581", {"start": v(-70.63, 98.87) * mm, "end": v(-70.95, 98.47) * mm});
            skLineSegment(sketch, "E582", {"start": v(-70.95, 98.47) * mm, "end": v(-71.28, 98.08) * mm});
            skLineSegment(sketch, "E583", {"start": v(-71.28, 98.08) * mm, "end": v(-71.63, 97.7) * mm});
            skLineSegment(sketch, "E584", {"start": v(-71.63, 97.7) * mm, "end": v(-71.98, 97.33) * mm});
            skLineSegment(sketch, "E585", {"start": v(-71.98, 97.33) * mm, "end": v(-72.28, 97.04) * mm});
            skLineSegment(sketch, "E586", {"start": v(-72.28, 97.04) * mm, "end": v(-72.58, 96.75) * mm});
            skLineSegment(sketch, "E587", {"start": v(-72.58, 96.75) * mm, "end": v(-72.88, 96.48) * mm});
            skLineSegment(sketch, "E588", {"start": v(-72.88, 96.48) * mm, "end": v(-73.2, 96.21) * mm});
            skLineSegment(sketch, "E589", {"start": v(-73.2, 96.21) * mm, "end": v(-73.52, 95.95) * mm});
            skLineSegment(sketch, "E590", {"start": v(-73.52, 95.95) * mm, "end": v(-73.84, 95.7) * mm});
            skLineSegment(sketch, "E591", {"start": v(-73.84, 95.7) * mm, "end": v(-74.17, 95.46) * mm});
            skLineSegment(sketch, "E592", {"start": v(-74.17, 95.46) * mm, "end": v(-74.51, 95.23) * mm});
            skLineSegment(sketch, "E593", {"start": v(-74.51, 95.23) * mm, "end": v(-74.85, 95) * mm});
            skLineSegment(sketch, "E594", {"start": v(-74.85, 95) * mm, "end": v(-75.2, 94.8) * mm});
            skLineSegment(sketch, "E595", {"start": v(-75.2, 94.8) * mm, "end": v(-75.55, 94.58) * mm});
            skLineSegment(sketch, "E596", {"start": v(-75.55, 94.58) * mm, "end": v(-75.9, 94.39) * mm});
            skLineSegment(sketch, "E597", {"start": v(-75.9, 94.39) * mm, "end": v(-76.27, 94.2) * mm});
            skLineSegment(sketch, "E598", {"start": v(-76.27, 94.2) * mm, "end": v(-76.64, 94.02) * mm});
            skLineSegment(sketch, "E599", {"start": v(-76.64, 94.02) * mm, "end": v(-77, 93.85) * mm});
            skLineSegment(sketch, "E600", {"start": v(-77, 93.85) * mm, "end": v(-77.38, 93.69) * mm});
            skLineSegment(sketch, "E601", {"start": v(-77.38, 93.69) * mm, "end": v(-77.76, 93.54) * mm});
            skLineSegment(sketch, "E602", {"start": v(-77.76, 93.54) * mm, "end": v(-78.14, 93.4) * mm});
            skLineSegment(sketch, "E603", {"start": v(-78.14, 93.4) * mm, "end": v(-78.53, 93.26) * mm});
            skLineSegment(sketch, "E604", {"start": v(-78.53, 93.26) * mm, "end": v(-78.92, 93.14) * mm});
            skLineSegment(sketch, "E605", {"start": v(-78.92, 93.14) * mm, "end": v(-79.3, 93.02) * mm});
            skLineSegment(sketch, "E606", {"start": v(-79.3, 93.02) * mm, "end": v(-79.7, 92.92) * mm});
            skLineSegment(sketch, "E607", {"start": v(-79.7, 92.92) * mm, "end": v(-80.1, 92.82) * mm});
            skLineSegment(sketch, "E608", {"start": v(-80.1, 92.82) * mm, "end": v(-80.5, 92.74) * mm});
            skLineSegment(sketch, "E609", {"start": v(-80.5, 92.74) * mm, "end": v(-80.9, 92.67) * mm});
            skLineSegment(sketch, "E610", {"start": v(-80.9, 92.67) * mm, "end": v(-81.3, 92.6) * mm});
            skLineSegment(sketch, "E611", {"start": v(-81.3, 92.6) * mm, "end": v(-81.71, 92.55) * mm});
            skLineSegment(sketch, "E612", {"start": v(-81.71, 92.55) * mm, "end": v(-82.12, 92.5) * mm});
            skLineSegment(sketch, "E613", {"start": v(-82.12, 92.5) * mm, "end": v(-82.53, 92.47) * mm});
            skLineSegment(sketch, "E614", {"start": v(-82.53, 92.47) * mm, "end": v(-82.95, 92.44) * mm});
            skLineSegment(sketch, "E615", {"start": v(-82.95, 92.44) * mm, "end": v(-83.36, 92.43) * mm});
            skLineSegment(sketch, "E616", {"start": v(-83.36, 92.43) * mm, "end": v(-83.77, 92.43) * mm});
            skLineSegment(sketch, "E617", {"start": v(-39.53, 92.43) * mm, "end": v(-39.95, 92.43) * mm});
            skLineSegment(sketch, "E618", {"start": v(-39.95, 92.43) * mm, "end": v(-40.37, 92.43) * mm});
            skLineSegment(sketch, "E619", {"start": v(-40.37, 92.43) * mm, "end": v(-40.78, 92.45) * mm});
            skLineSegment(sketch, "E620", {"start": v(-40.78, 92.45) * mm, "end": v(-41.2, 92.48) * mm});
            skLineSegment(sketch, "E621", {"start": v(-41.2, 92.48) * mm, "end": v(-41.61, 92.52) * mm});
            skLineSegment(sketch, "E622", {"start": v(-41.61, 92.52) * mm, "end": v(-42.03, 92.57) * mm});
            skLineSegment(sketch, "E623", {"start": v(-42.03, 92.57) * mm, "end": v(-42.44, 92.63) * mm});
            skLineSegment(sketch, "E624", {"start": v(-42.44, 92.63) * mm, "end": v(-42.85, 92.7) * mm});
            skLineSegment(sketch, "E625", {"start": v(-42.85, 92.7) * mm, "end": v(-43.26, 92.77) * mm});
            skLineSegment(sketch, "E626", {"start": v(-43.26, 92.77) * mm, "end": v(-43.66, 92.86) * mm});
            skLineSegment(sketch, "E627", {"start": v(-43.66, 92.86) * mm, "end": v(-44.06, 92.96) * mm});
            skLineSegment(sketch, "E628", {"start": v(-44.06, 92.96) * mm, "end": v(-44.46, 93.07) * mm});
            skLineSegment(sketch, "E629", {"start": v(-44.46, 93.07) * mm, "end": v(-44.86, 93.2) * mm});
            skLineSegment(sketch, "E630", {"start": v(-44.86, 93.2) * mm, "end": v(-45.25, 93.32) * mm});
            skLineSegment(sketch, "E631", {"start": v(-45.25, 93.32) * mm, "end": v(-45.64, 93.46) * mm});
            skLineSegment(sketch, "E632", {"start": v(-45.64, 93.46) * mm, "end": v(-46.03, 93.6) * mm});
            skLineSegment(sketch, "E633", {"start": v(-46.03, 93.6) * mm, "end": v(-46.41, 93.77) * mm});
            skLineSegment(sketch, "E634", {"start": v(-46.41, 93.77) * mm, "end": v(-46.79, 93.93) * mm});
            skLineSegment(sketch, "E635", {"start": v(-46.79, 93.93) * mm, "end": v(-47.16, 94.11) * mm});
            skLineSegment(sketch, "E636", {"start": v(-47.16, 94.11) * mm, "end": v(-47.53, 94.3) * mm});
            skLineSegment(sketch, "E637", {"start": v(-47.53, 94.3) * mm, "end": v(-47.9, 94.5) * mm});
            skLineSegment(sketch, "E638", {"start": v(-47.9, 94.5) * mm, "end": v(-48.26, 94.7) * mm});
            skLineSegment(sketch, "E639", {"start": v(-48.26, 94.7) * mm, "end": v(-48.61, 94.9) * mm});
            skLineSegment(sketch, "E640", {"start": v(-48.61, 94.9) * mm, "end": v(-48.97, 95.13) * mm});
            skLineSegment(sketch, "E641", {"start": v(-48.97, 95.13) * mm, "end": v(-49.31, 95.36) * mm});
            skLineSegment(sketch, "E642", {"start": v(-49.31, 95.36) * mm, "end": v(-49.65, 95.6) * mm});
            skLineSegment(sketch, "E643", {"start": v(-49.65, 95.6) * mm, "end": v(-49.98, 95.85) * mm});
            skLineSegment(sketch, "E644", {"start": v(-49.98, 95.85) * mm, "end": v(-50.31, 96.1) * mm});
            skLineSegment(sketch, "E645", {"start": v(-50.31, 96.1) * mm, "end": v(-50.63, 96.37) * mm});
            skLineSegment(sketch, "E646", {"start": v(-50.63, 96.37) * mm, "end": v(-50.95, 96.65) * mm});
            skLineSegment(sketch, "E647", {"start": v(-50.95, 96.65) * mm, "end": v(-51.26, 96.93) * mm});
            skLineSegment(sketch, "E648", {"start": v(-51.26, 96.93) * mm, "end": v(-51.56, 97.22) * mm});
            skLineSegment(sketch, "E649", {"start": v(-51.56, 97.22) * mm, "end": v(-51.91, 97.6) * mm});
            skLineSegment(sketch, "E650", {"start": v(-51.91, 97.6) * mm, "end": v(-52.25, 98) * mm});
            skLineSegment(sketch, "E651", {"start": v(-52.25, 98) * mm, "end": v(-52.58, 98.39) * mm});
            skLineSegment(sketch, "E652", {"start": v(-52.58, 98.39) * mm, "end": v(-52.9, 98.8) * mm});
            skLineSegment(sketch, "E653", {"start": v(-52.9, 98.8) * mm, "end": v(-53.2, 99.2) * mm});
            skLineSegment(sketch, "E654", {"start": v(-53.2, 99.2) * mm, "end": v(-53.5, 99.62) * mm});
            skLineSegment(sketch, "E655", {"start": v(-53.5, 99.62) * mm, "end": v(-53.79, 100.04) * mm});
            skLineSegment(sketch, "E656", {"start": v(-53.79, 100.04) * mm, "end": v(-54.07, 100.47) * mm});
            skLineSegment(sketch, "E657", {"start": v(-54.07, 100.47) * mm, "end": v(-54.33, 100.91) * mm});
            skLineSegment(sketch, "E658", {"start": v(-54.33, 100.91) * mm, "end": v(-54.58, 101.35) * mm});
            skLineSegment(sketch, "E659", {"start": v(-54.58, 101.35) * mm, "end": v(-54.83, 101.8) * mm});
            skLineSegment(sketch, "E660", {"start": v(-54.83, 101.8) * mm, "end": v(-55.06, 102.26) * mm});
            skLineSegment(sketch, "E661", {"start": v(-55.06, 102.26) * mm, "end": v(-55.28, 102.72) * mm});
            skLineSegment(sketch, "E662", {"start": v(-55.28, 102.72) * mm, "end": v(-55.49, 103.18) * mm});
            skLineSegment(sketch, "E663", {"start": v(-55.49, 103.18) * mm, "end": v(-55.68, 103.65) * mm});
            skLineSegment(sketch, "E664", {"start": v(-55.68, 103.65) * mm, "end": v(-55.87, 104.13) * mm});
            skLineSegment(sketch, "E665", {"start": v(-55.87, 104.13) * mm, "end": v(-56.04, 104.6) * mm});
            skLineSegment(sketch, "E666", {"start": v(-56.04, 104.6) * mm, "end": v(-56.2, 105.09) * mm});
            skLineSegment(sketch, "E667", {"start": v(-56.2, 105.09) * mm, "end": v(-56.35, 105.57) * mm});
            skLineSegment(sketch, "E668", {"start": v(-56.35, 105.57) * mm, "end": v(-56.5, 106.06) * mm});
            skLineSegment(sketch, "E669", {"start": v(-56.5, 106.06) * mm, "end": v(-56.62, 106.56) * mm});
            skLineSegment(sketch, "E670", {"start": v(-56.62, 106.56) * mm, "end": v(-56.73, 107.06) * mm});
            skLineSegment(sketch, "E671", {"start": v(-56.73, 107.06) * mm, "end": v(-56.83, 107.56) * mm});
            skLineSegment(sketch, "E672", {"start": v(-56.83, 107.56) * mm, "end": v(-56.92, 108.06) * mm});
            skLineSegment(sketch, "E673", {"start": v(-56.92, 108.06) * mm, "end": v(-57, 108.56) * mm});
            skLineSegment(sketch, "E674", {"start": v(-57, 108.56) * mm, "end": v(-57.07, 109.07) * mm});
            skLineSegment(sketch, "E675", {"start": v(-57.07, 109.07) * mm, "end": v(-57.12, 109.58) * mm});
            skLineSegment(sketch, "E676", {"start": v(-57.12, 109.58) * mm, "end": v(-57.16, 110.1) * mm});
            skLineSegment(sketch, "E677", {"start": v(-57.16, 110.1) * mm, "end": v(-57.18, 110.6) * mm});
            skLineSegment(sketch, "E678", {"start": v(-57.18, 110.6) * mm, "end": v(-57.2, 111.12) * mm});
            skLineSegment(sketch, "E679", {"start": v(-57.2, 111.12) * mm, "end": v(-57.2, 111.64) * mm});
            skLineSegment(sketch, "E680", {"start": v(-57.2, 111.64) * mm, "end": v(-57.19, 112.15) * mm});
            skLineSegment(sketch, "E681", {"start": v(-57.19, 112.15) * mm, "end": v(-57.2, 112.71) * mm});
            skLineSegment(sketch, "E682", {"start": v(-57.2, 112.71) * mm, "end": v(-57.2, 113.28) * mm});
            skLineSegment(sketch, "E683", {"start": v(-57.2, 113.28) * mm, "end": v(-57.2, 113.83) * mm});
            skLineSegment(sketch, "E684", {"start": v(-57.2, 113.83) * mm, "end": v(-57.17, 114.4) * mm});
            skLineSegment(sketch, "E685", {"start": v(-57.17, 114.4) * mm, "end": v(-57.13, 114.95) * mm});
            skLineSegment(sketch, "E686", {"start": v(-57.13, 114.95) * mm, "end": v(-57.07, 115.5) * mm});
            skLineSegment(sketch, "E687", {"start": v(-57.07, 115.5) * mm, "end": v(-57, 116.05) * mm});
            skLineSegment(sketch, "E688", {"start": v(-57, 116.05) * mm, "end": v(-56.92, 116.6) * mm});
            skLineSegment(sketch, "E689", {"start": v(-56.92, 116.6) * mm, "end": v(-56.83, 117.15) * mm});
            skLineSegment(sketch, "E690", {"start": v(-56.83, 117.15) * mm, "end": v(-56.72, 117.7) * mm});
            skLineSegment(sketch, "E691", {"start": v(-56.72, 117.7) * mm, "end": v(-56.6, 118.23) * mm});
            skLineSegment(sketch, "E692", {"start": v(-56.6, 118.23) * mm, "end": v(-56.46, 118.77) * mm});
            skLineSegment(sketch, "E693", {"start": v(-56.46, 118.77) * mm, "end": v(-56.3, 119.3) * mm});
            skLineSegment(sketch, "E694", {"start": v(-56.3, 119.3) * mm, "end": v(-56.15, 119.83) * mm});
            skLineSegment(sketch, "E695", {"start": v(-56.15, 119.83) * mm, "end": v(-55.97, 120.35) * mm});
            skLineSegment(sketch, "E696", {"start": v(-55.97, 120.35) * mm, "end": v(-55.78, 120.87) * mm});
            skLineSegment(sketch, "E697", {"start": v(-55.78, 120.87) * mm, "end": v(-55.58, 121.39) * mm});
            skLineSegment(sketch, "E698", {"start": v(-55.58, 121.39) * mm, "end": v(-55.37, 121.9) * mm});
            skLineSegment(sketch, "E699", {"start": v(-55.37, 121.9) * mm, "end": v(-55.14, 122.4) * mm});
            skLineSegment(sketch, "E700", {"start": v(-55.14, 122.4) * mm, "end": v(-54.9, 122.9) * mm});
            skLineSegment(sketch, "E701", {"start": v(-54.9, 122.9) * mm, "end": v(-54.65, 123.4) * mm});
            skLineSegment(sketch, "E702", {"start": v(-54.65, 123.4) * mm, "end": v(-54.39, 123.88) * mm});
            skLineSegment(sketch, "E703", {"start": v(-54.39, 123.88) * mm, "end": v(-54.11, 124.36) * mm});
            skLineSegment(sketch, "E704", {"start": v(-54.11, 124.36) * mm, "end": v(-53.83, 124.84) * mm});
            skLineSegment(sketch, "E705", {"start": v(-53.83, 124.84) * mm, "end": v(-53.53, 125.3) * mm});
            skLineSegment(sketch, "E706", {"start": v(-53.53, 125.3) * mm, "end": v(-53.21, 125.77) * mm});
            skLineSegment(sketch, "E707", {"start": v(-53.21, 125.77) * mm, "end": v(-52.9, 126.22) * mm});
            skLineSegment(sketch, "E708", {"start": v(-52.9, 126.22) * mm, "end": v(-52.55, 126.66) * mm});
            skLineSegment(sketch, "E709", {"start": v(-52.55, 126.66) * mm, "end": v(-52.2, 127.1) * mm});
            skLineSegment(sketch, "E710", {"start": v(-52.2, 127.1) * mm, "end": v(-51.85, 127.53) * mm});
            skLineSegment(sketch, "E711", {"start": v(-51.85, 127.53) * mm, "end": v(-51.48, 127.95) * mm});
            skLineSegment(sketch, "E712", {"start": v(-51.48, 127.95) * mm, "end": v(-51.1, 128.36) * mm});
            skLineSegment(sketch, "E713", {"start": v(-51.1, 128.36) * mm, "end": v(-50.81, 128.65) * mm});
            skLineSegment(sketch, "E714", {"start": v(-50.81, 128.65) * mm, "end": v(-50.52, 128.93) * mm});
            skLineSegment(sketch, "E715", {"start": v(-50.52, 128.93) * mm, "end": v(-50.22, 129.2) * mm});
            skLineSegment(sketch, "E716", {"start": v(-50.22, 129.2) * mm, "end": v(-49.91, 129.47) * mm});
            skLineSegment(sketch, "E717", {"start": v(-49.91, 129.47) * mm, "end": v(-49.6, 129.73) * mm});
            skLineSegment(sketch, "E718", {"start": v(-49.6, 129.73) * mm, "end": v(-49.28, 129.98) * mm});
            skLineSegment(sketch, "E719", {"start": v(-49.28, 129.98) * mm, "end": v(-48.96, 130.22) * mm});
            skLineSegment(sketch, "E720", {"start": v(-48.96, 130.22) * mm, "end": v(-48.63, 130.45) * mm});
            skLineSegment(sketch, "E721", {"start": v(-48.63, 130.45) * mm, "end": v(-48.3, 130.68) * mm});
            skLineSegment(sketch, "E722", {"start": v(-48.3, 130.68) * mm, "end": v(-47.95, 130.89) * mm});
            skLineSegment(sketch, "E723", {"start": v(-47.95, 130.89) * mm, "end": v(-47.6, 131.1) * mm});
            skLineSegment(sketch, "E724", {"start": v(-47.6, 131.1) * mm, "end": v(-47.26, 131.3) * mm});
            skLineSegment(sketch, "E725", {"start": v(-47.26, 131.3) * mm, "end": v(-46.9, 131.48) * mm});
            skLineSegment(sketch, "E726", {"start": v(-46.9, 131.48) * mm, "end": v(-46.54, 131.65) * mm});
            skLineSegment(sketch, "E727", {"start": v(-46.54, 131.65) * mm, "end": v(-46.18, 131.82) * mm});
            skLineSegment(sketch, "E728", {"start": v(-46.18, 131.82) * mm, "end": v(-45.81, 131.98) * mm});
            skLineSegment(sketch, "E729", {"start": v(-45.81, 131.98) * mm, "end": v(-45.44, 132.13) * mm});
            skLineSegment(sketch, "E730", {"start": v(-45.44, 132.13) * mm, "end": v(-45.06, 132.27) * mm});
            skLineSegment(sketch, "E731", {"start": v(-45.06, 132.27) * mm, "end": v(-44.68, 132.4) * mm});
            skLineSegment(sketch, "E732", {"start": v(-44.68, 132.4) * mm, "end": v(-44.3, 132.52) * mm});
            skLineSegment(sketch, "E733", {"start": v(-44.3, 132.52) * mm, "end": v(-43.91, 132.63) * mm});
            skLineSegment(sketch, "E734", {"start": v(-43.91, 132.63) * mm, "end": v(-43.53, 132.74) * mm});
            skLineSegment(sketch, "E735", {"start": v(-43.53, 132.74) * mm, "end": v(-43.13, 132.83) * mm});
            skLineSegment(sketch, "E736", {"start": v(-43.13, 132.83) * mm, "end": v(-42.74, 132.9) * mm});
            skLineSegment(sketch, "E737", {"start": v(-42.74, 132.9) * mm, "end": v(-42.34, 132.98) * mm});
            skLineSegment(sketch, "E738", {"start": v(-42.34, 132.98) * mm, "end": v(-41.94, 133.04) * mm});
            skLineSegment(sketch, "E739", {"start": v(-41.94, 133.04) * mm, "end": v(-41.54, 133.1) * mm});
            skLineSegment(sketch, "E740", {"start": v(-41.54, 133.1) * mm, "end": v(-41.14, 133.13) * mm});
            skLineSegment(sketch, "E741", {"start": v(-41.14, 133.13) * mm, "end": v(-40.74, 133.16) * mm});
            skLineSegment(sketch, "E742", {"start": v(-40.74, 133.16) * mm, "end": v(-40.33, 133.18) * mm});
            skLineSegment(sketch, "E743", {"start": v(-40.33, 133.18) * mm, "end": v(-39.93, 133.2) * mm});
            skLineSegment(sketch, "E744", {"start": v(-39.93, 133.2) * mm, "end": v(-39.52, 133.19) * mm});
            skLineSegment(sketch, "E745", {"start": v(-39.52, 133.19) * mm, "end": v(-39.1, 133.18) * mm});
            skLineSegment(sketch, "E746", {"start": v(-39.1, 133.18) * mm, "end": v(-38.7, 133.17) * mm});
            skLineSegment(sketch, "E747", {"start": v(-38.7, 133.17) * mm, "end": v(-38.28, 133.15) * mm});
            skLineSegment(sketch, "E748", {"start": v(-38.28, 133.15) * mm, "end": v(-37.87, 133.1) * mm});
            skLineSegment(sketch, "E749", {"start": v(-37.87, 133.1) * mm, "end": v(-37.46, 133.06) * mm});
            skLineSegment(sketch, "E750", {"start": v(-37.46, 133.06) * mm, "end": v(-37.05, 133) * mm});
            skLineSegment(sketch, "E751", {"start": v(-37.05, 133) * mm, "end": v(-36.65, 132.94) * mm});
            skLineSegment(sketch, "E752", {"start": v(-36.65, 132.94) * mm, "end": v(-36.25, 132.86) * mm});
            skLineSegment(sketch, "E753", {"start": v(-36.25, 132.86) * mm, "end": v(-35.85, 132.77) * mm});
            skLineSegment(sketch, "E754", {"start": v(-35.85, 132.77) * mm, "end": v(-35.45, 132.68) * mm});
            skLineSegment(sketch, "E755", {"start": v(-35.45, 132.68) * mm, "end": v(-35.06, 132.57) * mm});
            skLineSegment(sketch, "E756", {"start": v(-35.06, 132.57) * mm, "end": v(-34.67, 132.45) * mm});
            skLineSegment(sketch, "E757", {"start": v(-34.67, 132.45) * mm, "end": v(-34.28, 132.32) * mm});
            skLineSegment(sketch, "E758", {"start": v(-34.28, 132.32) * mm, "end": v(-33.9, 132.19) * mm});
            skLineSegment(sketch, "E759", {"start": v(-33.9, 132.19) * mm, "end": v(-33.51, 132.04) * mm});
            skLineSegment(sketch, "E760", {"start": v(-33.51, 132.04) * mm, "end": v(-33.14, 131.88) * mm});
            skLineSegment(sketch, "E761", {"start": v(-33.14, 131.88) * mm, "end": v(-32.77, 131.72) * mm});
            skLineSegment(sketch, "E762", {"start": v(-32.77, 131.72) * mm, "end": v(-32.4, 131.54) * mm});
            skLineSegment(sketch, "E763", {"start": v(-32.4, 131.54) * mm, "end": v(-32.03, 131.36) * mm});
            skLineSegment(sketch, "E764", {"start": v(-32.03, 131.36) * mm, "end": v(-31.68, 131.16) * mm});
            skLineSegment(sketch, "E765", {"start": v(-31.68, 131.16) * mm, "end": v(-31.32, 130.96) * mm});
            skLineSegment(sketch, "E766", {"start": v(-31.32, 130.96) * mm, "end": v(-30.97, 130.75) * mm});
            skLineSegment(sketch, "E767", {"start": v(-30.97, 130.75) * mm, "end": v(-30.63, 130.52) * mm});
            skLineSegment(sketch, "E768", {"start": v(-30.63, 130.52) * mm, "end": v(-30.3, 130.3) * mm});
            skLineSegment(sketch, "E769", {"start": v(-30.3, 130.3) * mm, "end": v(-29.96, 130.05) * mm});
            skLineSegment(sketch, "E770", {"start": v(-29.96, 130.05) * mm, "end": v(-29.63, 129.8) * mm});
            skLineSegment(sketch, "E771", {"start": v(-29.63, 129.8) * mm, "end": v(-29.31, 129.55) * mm});
            skLineSegment(sketch, "E772", {"start": v(-29.31, 129.55) * mm, "end": v(-29, 129.28) * mm});
            skLineSegment(sketch, "E773", {"start": v(-29, 129.28) * mm, "end": v(-28.7, 129) * mm});
            skLineSegment(sketch, "E774", {"start": v(-28.7, 129) * mm, "end": v(-28.39, 128.73) * mm});
            skLineSegment(sketch, "E775", {"start": v(-28.39, 128.73) * mm, "end": v(-28.1, 128.44) * mm});
            skLineSegment(sketch, "E776", {"start": v(-28.1, 128.44) * mm, "end": v(-27.8, 128.14) * mm});
            skLineSegment(sketch, "E777", {"start": v(-27.8, 128.14) * mm, "end": v(-27.44, 127.73) * mm});
            skLineSegment(sketch, "E778", {"start": v(-27.44, 127.73) * mm, "end": v(-27.08, 127.31) * mm});
            skLineSegment(sketch, "E779", {"start": v(-27.08, 127.31) * mm, "end": v(-26.73, 126.88) * mm});
            skLineSegment(sketch, "E780", {"start": v(-26.73, 126.88) * mm, "end": v(-26.4, 126.45) * mm});
            skLineSegment(sketch, "E781", {"start": v(-26.4, 126.45) * mm, "end": v(-26.07, 126) * mm});
            skLineSegment(sketch, "E782", {"start": v(-26.07, 126) * mm, "end": v(-25.76, 125.56) * mm});
            skLineSegment(sketch, "E783", {"start": v(-25.76, 125.56) * mm, "end": v(-25.46, 125.1) * mm});
            skLineSegment(sketch, "E784", {"start": v(-25.46, 125.1) * mm, "end": v(-25.17, 124.64) * mm});
            skLineSegment(sketch, "E785", {"start": v(-25.17, 124.64) * mm, "end": v(-24.89, 124.17) * mm});
            skLineSegment(sketch, "E786", {"start": v(-24.89, 124.17) * mm, "end": v(-24.62, 123.7) * mm});
            skLineSegment(sketch, "E787", {"start": v(-24.62, 123.7) * mm, "end": v(-24.37, 123.21) * mm});
            skLineSegment(sketch, "E788", {"start": v(-24.37, 123.21) * mm, "end": v(-24.13, 122.73) * mm});
            skLineSegment(sketch, "E789", {"start": v(-24.13, 122.73) * mm, "end": v(-23.9, 122.23) * mm});
            skLineSegment(sketch, "E790", {"start": v(-23.9, 122.23) * mm, "end": v(-23.68, 121.73) * mm});
            skLineSegment(sketch, "E791", {"start": v(-23.68, 121.73) * mm, "end": v(-23.47, 121.23) * mm});
            skLineSegment(sketch, "E792", {"start": v(-23.47, 121.23) * mm, "end": v(-23.28, 120.72) * mm});
            skLineSegment(sketch, "E793", {"start": v(-23.28, 120.72) * mm, "end": v(-23.1, 120.2) * mm});
            skLineSegment(sketch, "E794", {"start": v(-23.1, 120.2) * mm, "end": v(-22.93, 119.69) * mm});
            skLineSegment(sketch, "E795", {"start": v(-22.93, 119.69) * mm, "end": v(-22.78, 119.17) * mm});
            skLineSegment(sketch, "E796", {"start": v(-22.78, 119.17) * mm, "end": v(-22.64, 118.64) * mm});
            skLineSegment(sketch, "E797", {"start": v(-22.64, 118.64) * mm, "end": v(-22.5, 118.11) * mm});
            skLineSegment(sketch, "E798", {"start": v(-22.5, 118.11) * mm, "end": v(-22.4, 117.58) * mm});
            skLineSegment(sketch, "E799", {"start": v(-22.4, 117.58) * mm, "end": v(-22.3, 117.05) * mm});
            skLineSegment(sketch, "E800", {"start": v(-22.3, 117.05) * mm, "end": v(-22.2, 116.5) * mm});
            skLineSegment(sketch, "E801", {"start": v(-22.2, 116.5) * mm, "end": v(-22.13, 115.97) * mm});
            skLineSegment(sketch, "E802", {"start": v(-22.13, 115.97) * mm, "end": v(-22.06, 115.42) * mm});
            skLineSegment(sketch, "E803", {"start": v(-22.06, 115.42) * mm, "end": v(-22.01, 114.88) * mm});
            skLineSegment(sketch, "E804", {"start": v(-22.01, 114.88) * mm, "end": v(-21.98, 114.33) * mm});
            skLineSegment(sketch, "E805", {"start": v(-21.98, 114.33) * mm, "end": v(-21.96, 113.78) * mm});
            skLineSegment(sketch, "E806", {"start": v(-21.96, 113.78) * mm, "end": v(-21.95, 113.23) * mm});
            skLineSegment(sketch, "E807", {"start": v(-21.95, 113.23) * mm, "end": v(-21.95, 112.68) * mm});
            skLineSegment(sketch, "E808", {"start": v(-21.95, 112.68) * mm, "end": v(-21.97, 112.13) * mm});
            skLineSegment(sketch, "E809", {"start": v(-21.97, 112.13) * mm, "end": v(-21.97, 111.61) * mm});
            skLineSegment(sketch, "E810", {"start": v(-21.97, 111.61) * mm, "end": v(-21.97, 111.1) * mm});
            skLineSegment(sketch, "E811", {"start": v(-21.97, 111.1) * mm, "end": v(-21.99, 110.59) * mm});
            skLineSegment(sketch, "E812", {"start": v(-21.99, 110.59) * mm, "end": v(-22.02, 110.08) * mm});
            skLineSegment(sketch, "E813", {"start": v(-22.02, 110.08) * mm, "end": v(-22.06, 109.57) * mm});
            skLineSegment(sketch, "E814", {"start": v(-22.06, 109.57) * mm, "end": v(-22.12, 109.06) * mm});
            skLineSegment(sketch, "E815", {"start": v(-22.12, 109.06) * mm, "end": v(-22.19, 108.56) * mm});
            skLineSegment(sketch, "E816", {"start": v(-22.19, 108.56) * mm, "end": v(-22.27, 108.05) * mm});
            skLineSegment(sketch, "E817", {"start": v(-22.27, 108.05) * mm, "end": v(-22.36, 107.55) * mm});
            skLineSegment(sketch, "E818", {"start": v(-22.36, 107.55) * mm, "end": v(-22.47, 107.06) * mm});
            skLineSegment(sketch, "E819", {"start": v(-22.47, 107.06) * mm, "end": v(-22.59, 106.56) * mm});
            skLineSegment(sketch, "E820", {"start": v(-22.59, 106.56) * mm, "end": v(-22.72, 106.07) * mm});
            skLineSegment(sketch, "E821", {"start": v(-22.72, 106.07) * mm, "end": v(-22.86, 105.58) * mm});
            skLineSegment(sketch, "E822", {"start": v(-22.86, 105.58) * mm, "end": v(-23.01, 105.1) * mm});
            skLineSegment(sketch, "E823", {"start": v(-23.01, 105.1) * mm, "end": v(-23.18, 104.62) * mm});
            skLineSegment(sketch, "E824", {"start": v(-23.18, 104.62) * mm, "end": v(-23.36, 104.15) * mm});
            skLineSegment(sketch, "E825", {"start": v(-23.36, 104.15) * mm, "end": v(-23.55, 103.68) * mm});
            skLineSegment(sketch, "E826", {"start": v(-23.55, 103.68) * mm, "end": v(-23.75, 103.2) * mm});
            skLineSegment(sketch, "E827", {"start": v(-23.75, 103.2) * mm, "end": v(-23.96, 102.75) * mm});
            skLineSegment(sketch, "E828", {"start": v(-23.96, 102.75) * mm, "end": v(-24.19, 102.3) * mm});
            skLineSegment(sketch, "E829", {"start": v(-24.19, 102.3) * mm, "end": v(-24.42, 101.84) * mm});
            skLineSegment(sketch, "E830", {"start": v(-24.42, 101.84) * mm, "end": v(-24.67, 101.4) * mm});
            skLineSegment(sketch, "E831", {"start": v(-24.67, 101.4) * mm, "end": v(-24.93, 100.96) * mm});
            skLineSegment(sketch, "E832", {"start": v(-24.93, 100.96) * mm, "end": v(-25.2, 100.53) * mm});
            skLineSegment(sketch, "E833", {"start": v(-25.2, 100.53) * mm, "end": v(-25.48, 100.1) * mm});
            skLineSegment(sketch, "E834", {"start": v(-25.48, 100.1) * mm, "end": v(-25.77, 99.69) * mm});
            skLineSegment(sketch, "E835", {"start": v(-25.77, 99.69) * mm, "end": v(-26.07, 99.27) * mm});
            skLineSegment(sketch, "E836", {"start": v(-26.07, 99.27) * mm, "end": v(-26.38, 98.87) * mm});
            skLineSegment(sketch, "E837", {"start": v(-26.38, 98.87) * mm, "end": v(-26.7, 98.47) * mm});
            skLineSegment(sketch, "E838", {"start": v(-26.7, 98.47) * mm, "end": v(-27.04, 98.08) * mm});
            skLineSegment(sketch, "E839", {"start": v(-27.04, 98.08) * mm, "end": v(-27.38, 97.7) * mm});
            skLineSegment(sketch, "E840", {"start": v(-27.38, 97.7) * mm, "end": v(-27.74, 97.33) * mm});
            skLineSegment(sketch, "E841", {"start": v(-27.74, 97.33) * mm, "end": v(-28.03, 97.04) * mm});
            skLineSegment(sketch, "E842", {"start": v(-28.03, 97.04) * mm, "end": v(-28.33, 96.75) * mm});
            skLineSegment(sketch, "E843", {"start": v(-28.33, 96.75) * mm, "end": v(-28.64, 96.48) * mm});
            skLineSegment(sketch, "E844", {"start": v(-28.64, 96.48) * mm, "end": v(-28.95, 96.21) * mm});
            skLineSegment(sketch, "E845", {"start": v(-28.95, 96.21) * mm, "end": v(-29.27, 95.95) * mm});
            skLineSegment(sketch, "E846", {"start": v(-29.27, 95.95) * mm, "end": v(-29.6, 95.7) * mm});
            skLineSegment(sketch, "E847", {"start": v(-29.6, 95.7) * mm, "end": v(-29.93, 95.46) * mm});
            skLineSegment(sketch, "E848", {"start": v(-29.93, 95.46) * mm, "end": v(-30.26, 95.23) * mm});
            skLineSegment(sketch, "E849", {"start": v(-30.26, 95.23) * mm, "end": v(-30.6, 95) * mm});
            skLineSegment(sketch, "E850", {"start": v(-30.6, 95) * mm, "end": v(-30.95, 94.8) * mm});
            skLineSegment(sketch, "E851", {"start": v(-30.95, 94.8) * mm, "end": v(-31.3, 94.58) * mm});
            skLineSegment(sketch, "E852", {"start": v(-31.3, 94.58) * mm, "end": v(-31.66, 94.39) * mm});
            skLineSegment(sketch, "E853", {"start": v(-31.66, 94.39) * mm, "end": v(-32.03, 94.2) * mm});
            skLineSegment(sketch, "E854", {"start": v(-32.03, 94.2) * mm, "end": v(-32.4, 94.02) * mm});
            skLineSegment(sketch, "E855", {"start": v(-32.4, 94.02) * mm, "end": v(-32.76, 93.85) * mm});
            skLineSegment(sketch, "E856", {"start": v(-32.76, 93.85) * mm, "end": v(-33.14, 93.69) * mm});
            skLineSegment(sketch, "E857", {"start": v(-33.14, 93.69) * mm, "end": v(-33.51, 93.54) * mm});
            skLineSegment(sketch, "E858", {"start": v(-33.51, 93.54) * mm, "end": v(-33.9, 93.4) * mm});
            skLineSegment(sketch, "E859", {"start": v(-33.9, 93.4) * mm, "end": v(-34.28, 93.26) * mm});
            skLineSegment(sketch, "E860", {"start": v(-34.28, 93.26) * mm, "end": v(-34.67, 93.14) * mm});
            skLineSegment(sketch, "E861", {"start": v(-34.67, 93.14) * mm, "end": v(-35.06, 93.02) * mm});
            skLineSegment(sketch, "E862", {"start": v(-35.06, 93.02) * mm, "end": v(-35.46, 92.92) * mm});
            skLineSegment(sketch, "E863", {"start": v(-35.46, 92.92) * mm, "end": v(-35.86, 92.82) * mm});
            skLineSegment(sketch, "E864", {"start": v(-35.86, 92.82) * mm, "end": v(-36.26, 92.74) * mm});
            skLineSegment(sketch, "E865", {"start": v(-36.26, 92.74) * mm, "end": v(-36.66, 92.67) * mm});
            skLineSegment(sketch, "E866", {"start": v(-36.66, 92.67) * mm, "end": v(-37.06, 92.6) * mm});
            skLineSegment(sketch, "E867", {"start": v(-37.06, 92.6) * mm, "end": v(-37.47, 92.55) * mm});
            skLineSegment(sketch, "E868", {"start": v(-37.47, 92.55) * mm, "end": v(-37.88, 92.5) * mm});
            skLineSegment(sketch, "E869", {"start": v(-37.88, 92.5) * mm, "end": v(-38.29, 92.47) * mm});
            skLineSegment(sketch, "E870", {"start": v(-38.29, 92.47) * mm, "end": v(-38.7, 92.44) * mm});
            skLineSegment(sketch, "E871", {"start": v(-38.7, 92.44) * mm, "end": v(-39.11, 92.43) * mm});
            skLineSegment(sketch, "E872", {"start": v(-39.11, 92.43) * mm, "end": v(-39.53, 92.43) * mm});
            skLineSegment(sketch, "E873", {"start": v(-12.95, 92.96) * mm, "end": v(-12.95, 132.96) * mm});
            skLineSegment(sketch, "E874", {"start": v(-12.95, 132.96) * mm, "end": v(11.91, 132.96) * mm});
            skLineSegment(sketch, "E875", {"start": v(-12.95, 113.85) * mm, "end": v(10.12, 113.85) * mm});
            skLineSegment(sketch, "E876", {"start": v(49.3, 124.35) * mm, "end": v(49.46, 124.87) * mm});
            skLineSegment(sketch, "E877", {"start": v(49.46, 124.87) * mm, "end": v(49.64, 125.38) * mm});
            skLineSegment(sketch, "E878", {"start": v(49.64, 125.38) * mm, "end": v(49.85, 125.88) * mm});
            skLineSegment(sketch, "E879", {"start": v(49.85, 125.88) * mm, "end": v(50.07, 126.36) * mm});
            skLineSegment(sketch, "E880", {"start": v(50.07, 126.36) * mm, "end": v(50.3, 126.84) * mm});
            skLineSegment(sketch, "E881", {"start": v(50.3, 126.84) * mm, "end": v(50.57, 127.3) * mm});
            skLineSegment(sketch, "E882", {"start": v(50.57, 127.3) * mm, "end": v(50.84, 127.75) * mm});
            skLineSegment(sketch, "E883", {"start": v(50.84, 127.75) * mm, "end": v(51.14, 128.19) * mm});
            skLineSegment(sketch, "E884", {"start": v(51.14, 128.19) * mm, "end": v(51.45, 128.61) * mm});
            skLineSegment(sketch, "E885", {"start": v(51.45, 128.61) * mm, "end": v(51.77, 129.02) * mm});
            skLineSegment(sketch, "E886", {"start": v(51.77, 129.02) * mm, "end": v(52.12, 129.42) * mm});
            skLineSegment(sketch, "E887", {"start": v(52.12, 129.42) * mm, "end": v(52.47, 129.8) * mm});
            skLineSegment(sketch, "E888", {"start": v(52.47, 129.8) * mm, "end": v(52.84, 130.17) * mm});
            skLineSegment(sketch, "E889", {"start": v(52.84, 130.17) * mm, "end": v(53.23, 130.52) * mm});
            skLineSegment(sketch, "E890", {"start": v(53.23, 130.52) * mm, "end": v(53.63, 130.86) * mm});
            skLineSegment(sketch, "E891", {"start": v(53.63, 130.86) * mm, "end": v(54.04, 131.18) * mm});
            skLineSegment(sketch, "E892", {"start": v(54.04, 131.18) * mm, "end": v(54.46, 131.48) * mm});
            skLineSegment(sketch, "E893", {"start": v(54.46, 131.48) * mm, "end": v(54.9, 131.77) * mm});
            skLineSegment(sketch, "E894", {"start": v(54.9, 131.77) * mm, "end": v(55.34, 132.04) * mm});
            skLineSegment(sketch, "E895", {"start": v(55.34, 132.04) * mm, "end": v(55.8, 132.29) * mm});
            skLineSegment(sketch, "E896", {"start": v(55.8, 132.29) * mm, "end": v(56.27, 132.52) * mm});
            skLineSegment(sketch, "E897", {"start": v(56.27, 132.52) * mm, "end": v(56.75, 132.74) * mm});
            skLineSegment(sketch, "E898", {"start": v(56.75, 132.74) * mm, "end": v(57.23, 132.94) * mm});
            skLineSegment(sketch, "E899", {"start": v(57.23, 132.94) * mm, "end": v(57.73, 133.11) * mm});
            skLineSegment(sketch, "E900", {"start": v(57.73, 133.11) * mm, "end": v(58.23, 133.27) * mm});
            skLineSegment(sketch, "E901", {"start": v(58.23, 133.27) * mm, "end": v(58.74, 133.4) * mm});
            skLineSegment(sketch, "E902", {"start": v(58.74, 133.4) * mm, "end": v(59.26, 133.52) * mm});
            skLineSegment(sketch, "E903", {"start": v(59.26, 133.52) * mm, "end": v(59.78, 133.62) * mm});
            skLineSegment(sketch, "E904", {"start": v(59.78, 133.62) * mm, "end": v(60.32, 133.7) * mm});
            skLineSegment(sketch, "E905", {"start": v(60.32, 133.7) * mm, "end": v(60.85, 133.75) * mm});
            skLineSegment(sketch, "E906", {"start": v(60.85, 133.75) * mm, "end": v(61.4, 133.78) * mm});
            skLineSegment(sketch, "E907", {"start": v(61.4, 133.78) * mm, "end": v(61.94, 133.79) * mm});
            skLineSegment(sketch, "E908", {"start": v(61.94, 133.79) * mm, "end": v(62.58, 133.78) * mm});
            skLineSegment(sketch, "E909", {"start": v(62.58, 133.78) * mm, "end": v(63.21, 133.74) * mm});
            skLineSegment(sketch, "E910", {"start": v(63.21, 133.74) * mm, "end": v(63.83, 133.68) * mm});
            skLineSegment(sketch, "E911", {"start": v(63.83, 133.68) * mm, "end": v(64.45, 133.6) * mm});
            skLineSegment(sketch, "E912", {"start": v(64.45, 133.6) * mm, "end": v(65.05, 133.5) * mm});
            skLineSegment(sketch, "E913", {"start": v(65.05, 133.5) * mm, "end": v(65.64, 133.37) * mm});
            skLineSegment(sketch, "E914", {"start": v(65.64, 133.37) * mm, "end": v(66.22, 133.23) * mm});
            skLineSegment(sketch, "E915", {"start": v(66.22, 133.23) * mm, "end": v(66.79, 133.06) * mm});
            skLineSegment(sketch, "E916", {"start": v(66.79, 133.06) * mm, "end": v(67.34, 132.87) * mm});
            skLineSegment(sketch, "E917", {"start": v(67.34, 132.87) * mm, "end": v(67.87, 132.67) * mm});
            skLineSegment(sketch, "E918", {"start": v(67.87, 132.67) * mm, "end": v(68.4, 132.44) * mm});
            skLineSegment(sketch, "E919", {"start": v(68.4, 132.44) * mm, "end": v(68.9, 132.2) * mm});
            skLineSegment(sketch, "E920", {"start": v(68.9, 132.2) * mm, "end": v(69.39, 131.94) * mm});
            skLineSegment(sketch, "E921", {"start": v(69.39, 131.94) * mm, "end": v(69.86, 131.67) * mm});
            skLineSegment(sketch, "E922", {"start": v(69.86, 131.67) * mm, "end": v(70.31, 131.38) * mm});
            skLineSegment(sketch, "E923", {"start": v(70.31, 131.38) * mm, "end": v(70.74, 131.07) * mm});
            skLineSegment(sketch, "E924", {"start": v(70.74, 131.07) * mm, "end": v(71.16, 130.75) * mm});
            skLineSegment(sketch, "E925", {"start": v(71.16, 130.75) * mm, "end": v(71.55, 130.41) * mm});
            skLineSegment(sketch, "E926", {"start": v(71.55, 130.41) * mm, "end": v(71.92, 130.06) * mm});
            skLineSegment(sketch, "E927", {"start": v(71.92, 130.06) * mm, "end": v(72.26, 129.7) * mm});
            skLineSegment(sketch, "E928", {"start": v(72.26, 129.7) * mm, "end": v(72.59, 129.32) * mm});
            skLineSegment(sketch, "E929", {"start": v(72.59, 129.32) * mm, "end": v(72.89, 128.93) * mm});
            skLineSegment(sketch, "E930", {"start": v(72.89, 128.93) * mm, "end": v(73.16, 128.53) * mm});
            skLineSegment(sketch, "E931", {"start": v(73.16, 128.53) * mm, "end": v(73.41, 128.12) * mm});
            skLineSegment(sketch, "E932", {"start": v(73.41, 128.12) * mm, "end": v(73.64, 127.7) * mm});
            skLineSegment(sketch, "E933", {"start": v(73.64, 127.7) * mm, "end": v(73.83, 127.27) * mm});
            skLineSegment(sketch, "E934", {"start": v(73.83, 127.27) * mm, "end": v(74, 126.83) * mm});
            skLineSegment(sketch, "E935", {"start": v(74, 126.83) * mm, "end": v(74.07, 126.6) * mm});
            skLineSegment(sketch, "E936", {"start": v(74.07, 126.6) * mm, "end": v(74.14, 126.38) * mm});
            skLineSegment(sketch, "E937", {"start": v(74.14, 126.38) * mm, "end": v(74.2, 126.15) * mm});
            skLineSegment(sketch, "E938", {"start": v(74.2, 126.15) * mm, "end": v(74.25, 125.92) * mm});
            skLineSegment(sketch, "E939", {"start": v(74.25, 125.92) * mm, "end": v(74.3, 125.7) * mm});
            skLineSegment(sketch, "E940", {"start": v(74.3, 125.7) * mm, "end": v(74.33, 125.46) * mm});
            skLineSegment(sketch, "E941", {"start": v(74.33, 125.46) * mm, "end": v(74.35, 125.22) * mm});
            skLineSegment(sketch, "E942", {"start": v(74.35, 125.22) * mm, "end": v(74.37, 124.99) * mm});
            skLineSegment(sketch, "E943", {"start": v(74.37, 124.99) * mm, "end": v(74.39, 124.75) * mm});
            skLineSegment(sketch, "E944", {"start": v(74.39, 124.75) * mm, "end": v(74.4, 124.5) * mm});
            skLineSegment(sketch, "E945", {"start": v(74.4, 124.5) * mm, "end": v(74.39, 124.25) * mm});
            skLineSegment(sketch, "E946", {"start": v(74.39, 124.25) * mm, "end": v(74.37, 124) * mm});
            skLineSegment(sketch, "E947", {"start": v(74.37, 124) * mm, "end": v(74.35, 123.75) * mm});
            skLineSegment(sketch, "E948", {"start": v(74.35, 123.75) * mm, "end": v(74.32, 123.5) * mm});
            skLineSegment(sketch, "E949", {"start": v(74.32, 123.5) * mm, "end": v(74.28, 123.24) * mm});
            skLineSegment(sketch, "E950", {"start": v(74.28, 123.24) * mm, "end": v(74.24, 123) * mm});
            skLineSegment(sketch, "E951", {"start": v(74.24, 123) * mm, "end": v(74.18, 122.75) * mm});
            skLineSegment(sketch, "E952", {"start": v(74.18, 122.75) * mm, "end": v(74.12, 122.5) * mm});
            skLineSegment(sketch, "E953", {"start": v(74.12, 122.5) * mm, "end": v(74.04, 122.27) * mm});
            skLineSegment(sketch, "E954", {"start": v(74.04, 122.27) * mm, "end": v(73.96, 122.03) * mm});
            skLineSegment(sketch, "E955", {"start": v(73.96, 122.03) * mm, "end": v(73.88, 121.8) * mm});
            skLineSegment(sketch, "E956", {"start": v(73.88, 121.8) * mm, "end": v(73.78, 121.56) * mm});
            skLineSegment(sketch, "E957", {"start": v(73.78, 121.56) * mm, "end": v(73.68, 121.33) * mm});
            skLineSegment(sketch, "E958", {"start": v(73.68, 121.33) * mm, "end": v(73.57, 121.1) * mm});
            skLineSegment(sketch, "E959", {"start": v(73.57, 121.1) * mm, "end": v(73.45, 120.87) * mm});
            skLineSegment(sketch, "E960", {"start": v(73.45, 120.87) * mm, "end": v(73.33, 120.65) * mm});
            skLineSegment(sketch, "E961", {"start": v(73.33, 120.65) * mm, "end": v(73.06, 120.2) * mm});
            skLineSegment(sketch, "E962", {"start": v(73.06, 120.2) * mm, "end": v(72.76, 119.78) * mm});
            skLineSegment(sketch, "E963", {"start": v(72.76, 119.78) * mm, "end": v(72.43, 119.36) * mm});
            skLineSegment(sketch, "E964", {"start": v(72.43, 119.36) * mm, "end": v(72.08, 118.96) * mm});
            skLineSegment(sketch, "E965", {"start": v(72.08, 118.96) * mm, "end": v(71.7, 118.57) * mm});
            skLineSegment(sketch, "E966", {"start": v(71.7, 118.57) * mm, "end": v(71.3, 118.2) * mm});
            skLineSegment(sketch, "E967", {"start": v(71.3, 118.2) * mm, "end": v(70.87, 117.84) * mm});
            skLineSegment(sketch, "E968", {"start": v(70.87, 117.84) * mm, "end": v(70.42, 117.5) * mm});
            skLineSegment(sketch, "E969", {"start": v(70.42, 117.5) * mm, "end": v(69.95, 117.17) * mm});
            skLineSegment(sketch, "E970", {"start": v(69.95, 117.17) * mm, "end": v(69.46, 116.85) * mm});
            skLineSegment(sketch, "E971", {"start": v(69.46, 116.85) * mm, "end": v(68.95, 116.56) * mm});
            skLineSegment(sketch, "E972", {"start": v(68.95, 116.56) * mm, "end": v(68.42, 116.28) * mm});
            skLineSegment(sketch, "E973", {"start": v(68.42, 116.28) * mm, "end": v(67.87, 116.02) * mm});
            skLineSegment(sketch, "E974", {"start": v(67.87, 116.02) * mm, "end": v(67.3, 115.79) * mm});
            skLineSegment(sketch, "E975", {"start": v(67.3, 115.79) * mm, "end": v(66.72, 115.57) * mm});
            skLineSegment(sketch, "E976", {"start": v(66.72, 115.57) * mm, "end": v(66.12, 115.37) * mm});
            skLineSegment(sketch, "E977", {"start": v(66.12, 115.37) * mm, "end": v(65.5, 115.2) * mm});
            skLineSegment(sketch, "E978", {"start": v(65.5, 115.2) * mm, "end": v(64.87, 115.03) * mm});
            skLineSegment(sketch, "E979", {"start": v(64.87, 115.03) * mm, "end": v(64.23, 114.9) * mm});
            skLineSegment(sketch, "E980", {"start": v(64.23, 114.9) * mm, "end": v(63.57, 114.79) * mm});
            skLineSegment(sketch, "E981", {"start": v(63.57, 114.79) * mm, "end": v(62.9, 114.7) * mm});
            skLineSegment(sketch, "E982", {"start": v(62.9, 114.7) * mm, "end": v(62.23, 114.64) * mm});
            skLineSegment(sketch, "E983", {"start": v(62.23, 114.64) * mm, "end": v(61.54, 114.6) * mm});
            skLineSegment(sketch, "E984", {"start": v(61.54, 114.6) * mm, "end": v(60.84, 114.59) * mm});
            skLineSegment(sketch, "E985", {"start": v(60.84, 114.59) * mm, "end": v(61.62, 114.57) * mm});
            skLineSegment(sketch, "E986", {"start": v(61.62, 114.57) * mm, "end": v(62.38, 114.53) * mm});
            skLineSegment(sketch, "E987", {"start": v(62.38, 114.53) * mm, "end": v(63.13, 114.47) * mm});
            skLineSegment(sketch, "E988", {"start": v(63.13, 114.47) * mm, "end": v(63.87, 114.37) * mm});
            skLineSegment(sketch, "E989", {"start": v(63.87, 114.37) * mm, "end": v(64.6, 114.26) * mm});
            skLineSegment(sketch, "E990", {"start": v(64.6, 114.26) * mm, "end": v(65.3, 114.11) * mm});
            skLineSegment(sketch, "E991", {"start": v(65.3, 114.11) * mm, "end": v(66, 113.95) * mm});
            skLineSegment(sketch, "E992", {"start": v(66, 113.95) * mm, "end": v(66.69, 113.76) * mm});
            skLineSegment(sketch, "E993", {"start": v(66.69, 113.76) * mm, "end": v(67.35, 113.55) * mm});
            skLineSegment(sketch, "E994", {"start": v(67.35, 113.55) * mm, "end": v(68, 113.31) * mm});
            skLineSegment(sketch, "E995", {"start": v(68, 113.31) * mm, "end": v(68.63, 113.06) * mm});
            skLineSegment(sketch, "E996", {"start": v(68.63, 113.06) * mm, "end": v(69.24, 112.78) * mm});
            skLineSegment(sketch, "E997", {"start": v(69.24, 112.78) * mm, "end": v(69.83, 112.5) * mm});
            skLineSegment(sketch, "E998", {"start": v(69.83, 112.5) * mm, "end": v(70.4, 112.18) * mm});
            skLineSegment(sketch, "E999", {"start": v(70.4, 112.18) * mm, "end": v(70.94, 111.85) * mm});
            skLineSegment(sketch, "E1000", {"start": v(70.94, 111.85) * mm, "end": v(71.46, 111.5) * mm});
            skLineSegment(sketch, "E1001", {"start": v(71.46, 111.5) * mm, "end": v(71.96, 111.13) * mm});
            skLineSegment(sketch, "E1002", {"start": v(71.96, 111.13) * mm, "end": v(72.43, 110.75) * mm});
            skLineSegment(sketch, "E1003", {"start": v(72.43, 110.75) * mm, "end": v(72.88, 110.35) * mm});
            skLineSegment(sketch, "E1004", {"start": v(72.88, 110.35) * mm, "end": v(73.3, 109.93) * mm});
            skLineSegment(sketch, "E1005", {"start": v(73.3, 109.93) * mm, "end": v(73.5, 109.72) * mm});
            skLineSegment(sketch, "E1006", {"start": v(73.5, 109.72) * mm, "end": v(73.68, 109.5) * mm});
            skLineSegment(sketch, "E1007", {"start": v(73.68, 109.5) * mm, "end": v(73.87, 109.28) * mm});
            skLineSegment(sketch, "E1008", {"start": v(73.87, 109.28) * mm, "end": v(74.05, 109.06) * mm});
            skLineSegment(sketch, "E1009", {"start": v(74.05, 109.06) * mm, "end": v(74.22, 108.84) * mm});
            skLineSegment(sketch, "E1010", {"start": v(74.22, 108.84) * mm, "end": v(74.38, 108.6) * mm});
            skLineSegment(sketch, "E1011", {"start": v(74.38, 108.6) * mm, "end": v(74.53, 108.37) * mm});
            skLineSegment(sketch, "E1012", {"start": v(74.53, 108.37) * mm, "end": v(74.68, 108.14) * mm});
            skLineSegment(sketch, "E1013", {"start": v(74.68, 108.14) * mm, "end": v(74.82, 107.9) * mm});
            skLineSegment(sketch, "E1014", {"start": v(74.82, 107.9) * mm, "end": v(74.95, 107.66) * mm});
            skLineSegment(sketch, "E1015", {"start": v(74.95, 107.66) * mm, "end": v(75.07, 107.42) * mm});
            skLineSegment(sketch, "E1016", {"start": v(75.07, 107.42) * mm, "end": v(75.18, 107.17) * mm});
            skLineSegment(sketch, "E1017", {"start": v(75.18, 107.17) * mm, "end": v(75.29, 106.92) * mm});
            skLineSegment(sketch, "E1018", {"start": v(75.29, 106.92) * mm, "end": v(75.39, 106.67) * mm});
            skLineSegment(sketch, "E1019", {"start": v(75.39, 106.67) * mm, "end": v(75.47, 106.41) * mm});
            skLineSegment(sketch, "E1020", {"start": v(75.47, 106.41) * mm, "end": v(75.55, 106.16) * mm});
            skLineSegment(sketch, "E1021", {"start": v(75.55, 106.16) * mm, "end": v(75.62, 105.9) * mm});
            skLineSegment(sketch, "E1022", {"start": v(75.62, 105.9) * mm, "end": v(75.68, 105.64) * mm});
            skLineSegment(sketch, "E1023", {"start": v(75.68, 105.64) * mm, "end": v(75.74, 105.37) * mm});
            skLineSegment(sketch, "E1024", {"start": v(75.74, 105.37) * mm, "end": v(75.78, 105.1) * mm});
            skLineSegment(sketch, "E1025", {"start": v(75.78, 105.1) * mm, "end": v(75.81, 104.84) * mm});
            skLineSegment(sketch, "E1026", {"start": v(75.81, 104.84) * mm, "end": v(75.84, 104.57) * mm});
            skLineSegment(sketch, "E1027", {"start": v(75.84, 104.57) * mm, "end": v(75.85, 104.3) * mm});
            skLineSegment(sketch, "E1028", {"start": v(75.85, 104.3) * mm, "end": v(75.86, 104.03) * mm});
            skLineSegment(sketch, "E1029", {"start": v(75.86, 104.03) * mm, "end": v(75.85, 103.72) * mm});
            skLineSegment(sketch, "E1030", {"start": v(75.85, 103.72) * mm, "end": v(75.84, 103.42) * mm});
            skLineSegment(sketch, "E1031", {"start": v(75.84, 103.42) * mm, "end": v(75.82, 103.12) * mm});
            skLineSegment(sketch, "E1032", {"start": v(75.82, 103.12) * mm, "end": v(75.8, 102.82) * mm});
            skLineSegment(sketch, "E1033", {"start": v(75.8, 102.82) * mm, "end": v(75.76, 102.52) * mm});
            skLineSegment(sketch, "E1034", {"start": v(75.76, 102.52) * mm, "end": v(75.72, 102.23) * mm});
            skLineSegment(sketch, "E1035", {"start": v(75.72, 102.23) * mm, "end": v(75.62, 101.64) * mm});
            skLineSegment(sketch, "E1036", {"start": v(75.62, 101.64) * mm, "end": v(75.48, 101.07) * mm});
            skLineSegment(sketch, "E1037", {"start": v(75.48, 101.07) * mm, "end": v(75.32, 100.5) * mm});
            skLineSegment(sketch, "E1038", {"start": v(75.32, 100.5) * mm, "end": v(75.14, 99.96) * mm});
            skLineSegment(sketch, "E1039", {"start": v(75.14, 99.96) * mm, "end": v(74.93, 99.42) * mm});
            skLineSegment(sketch, "E1040", {"start": v(74.93, 99.42) * mm, "end": v(74.69, 98.9) * mm});
            skLineSegment(sketch, "E1041", {"start": v(74.69, 98.9) * mm, "end": v(74.43, 98.39) * mm});
            skLineSegment(sketch, "E1042", {"start": v(74.43, 98.39) * mm, "end": v(74.14, 97.9) * mm});
            skLineSegment(sketch, "E1043", {"start": v(74.14, 97.9) * mm, "end": v(73.83, 97.41) * mm});
            skLineSegment(sketch, "E1044", {"start": v(73.83, 97.41) * mm, "end": v(73.5, 96.95) * mm});
            skLineSegment(sketch, "E1045", {"start": v(73.5, 96.95) * mm, "end": v(73.15, 96.5) * mm});
            skLineSegment(sketch, "E1046", {"start": v(73.15, 96.5) * mm, "end": v(72.78, 96.07) * mm});
            skLineSegment(sketch, "E1047", {"start": v(72.78, 96.07) * mm, "end": v(72.39, 95.66) * mm});
            skLineSegment(sketch, "E1048", {"start": v(72.39, 95.66) * mm, "end": v(71.98, 95.27) * mm});
            skLineSegment(sketch, "E1049", {"start": v(71.98, 95.27) * mm, "end": v(71.55, 94.9) * mm});
            skLineSegment(sketch, "E1050", {"start": v(71.55, 94.9) * mm, "end": v(71.1, 94.54) * mm});
            skLineSegment(sketch, "E1051", {"start": v(71.1, 94.54) * mm, "end": v(70.64, 94.21) * mm});
            skLineSegment(sketch, "E1052", {"start": v(70.64, 94.21) * mm, "end": v(70.15, 93.9) * mm});
            skLineSegment(sketch, "E1053", {"start": v(70.15, 93.9) * mm, "end": v(69.66, 93.62) * mm});
            skLineSegment(sketch, "E1054", {"start": v(69.66, 93.62) * mm, "end": v(69.15, 93.36) * mm});
            skLineSegment(sketch, "E1055", {"start": v(69.15, 93.36) * mm, "end": v(68.62, 93.12) * mm});
            skLineSegment(sketch, "E1056", {"start": v(68.62, 93.12) * mm, "end": v(68.09, 92.9) * mm});
            skLineSegment(sketch, "E1057", {"start": v(68.09, 92.9) * mm, "end": v(67.54, 92.72) * mm});
            skLineSegment(sketch, "E1058", {"start": v(67.54, 92.72) * mm, "end": v(66.97, 92.56) * mm});
            skLineSegment(sketch, "E1059", {"start": v(66.97, 92.56) * mm, "end": v(66.4, 92.43) * mm});
            skLineSegment(sketch, "E1060", {"start": v(66.4, 92.43) * mm, "end": v(65.82, 92.33) * mm});
            skLineSegment(sketch, "E1061", {"start": v(65.82, 92.33) * mm, "end": v(65.52, 92.28) * mm});
            skLineSegment(sketch, "E1062", {"start": v(65.52, 92.28) * mm, "end": v(65.23, 92.25) * mm});
            skLineSegment(sketch, "E1063", {"start": v(65.23, 92.25) * mm, "end": v(64.93, 92.22) * mm});
            skLineSegment(sketch, "E1064", {"start": v(64.93, 92.22) * mm, "end": v(64.63, 92.2) * mm});
            skLineSegment(sketch, "E1065", {"start": v(64.63, 92.2) * mm, "end": v(64.32, 92.2) * mm});
            skLineSegment(sketch, "E1066", {"start": v(64.32, 92.2) * mm, "end": v(64.02, 92.19) * mm});
            skLineSegment(sketch, "E1067", {"start": v(64.02, 92.19) * mm, "end": v(62.58, 92.19) * mm});
            skLineSegment(sketch, "E1068", {"start": v(62.58, 92.19) * mm, "end": v(61.92, 92.2) * mm});
            skLineSegment(sketch, "E1069", {"start": v(61.92, 92.2) * mm, "end": v(61.26, 92.24) * mm});
            skLineSegment(sketch, "E1070", {"start": v(61.26, 92.24) * mm, "end": v(60.61, 92.3) * mm});
            skLineSegment(sketch, "E1071", {"start": v(60.61, 92.3) * mm, "end": v(59.97, 92.4) * mm});
            skLineSegment(sketch, "E1072", {"start": v(59.97, 92.4) * mm, "end": v(59.33, 92.52) * mm});
            skLineSegment(sketch, "E1073", {"start": v(59.33, 92.52) * mm, "end": v(58.7, 92.66) * mm});
            skLineSegment(sketch, "E1074", {"start": v(58.7, 92.66) * mm, "end": v(58.08, 92.82) * mm});
            skLineSegment(sketch, "E1075", {"start": v(58.08, 92.82) * mm, "end": v(57.47, 93.01) * mm});
            skLineSegment(sketch, "E1076", {"start": v(57.47, 93.01) * mm, "end": v(56.87, 93.23) * mm});
            skLineSegment(sketch, "E1077", {"start": v(56.87, 93.23) * mm, "end": v(56.28, 93.46) * mm});
            skLineSegment(sketch, "E1078", {"start": v(56.28, 93.46) * mm, "end": v(55.7, 93.72) * mm});
            skLineSegment(sketch, "E1079", {"start": v(55.7, 93.72) * mm, "end": v(55.12, 94) * mm});
            skLineSegment(sketch, "E1080", {"start": v(55.12, 94) * mm, "end": v(54.57, 94.3) * mm});
            skLineSegment(sketch, "E1081", {"start": v(54.57, 94.3) * mm, "end": v(54.02, 94.63) * mm});
            skLineSegment(sketch, "E1082", {"start": v(54.02, 94.63) * mm, "end": v(53.49, 94.97) * mm});
            skLineSegment(sketch, "E1083", {"start": v(53.49, 94.97) * mm, "end": v(52.97, 95.34) * mm});
            skLineSegment(sketch, "E1084", {"start": v(52.97, 95.34) * mm, "end": v(52.46, 95.72) * mm});
            skLineSegment(sketch, "E1085", {"start": v(52.46, 95.72) * mm, "end": v(51.97, 96.13) * mm});
            skLineSegment(sketch, "E1086", {"start": v(51.97, 96.13) * mm, "end": v(51.5, 96.55) * mm});
            skLineSegment(sketch, "E1087", {"start": v(51.5, 96.55) * mm, "end": v(51.04, 96.99) * mm});
            skLineSegment(sketch, "E1088", {"start": v(51.04, 96.99) * mm, "end": v(50.6, 97.45) * mm});
            skLineSegment(sketch, "E1089", {"start": v(50.6, 97.45) * mm, "end": v(50.18, 97.92) * mm});
            skLineSegment(sketch, "E1090", {"start": v(50.18, 97.92) * mm, "end": v(49.77, 98.42) * mm});
            skLineSegment(sketch, "E1091", {"start": v(49.77, 98.42) * mm, "end": v(49.39, 98.93) * mm});
            skLineSegment(sketch, "E1092", {"start": v(49.39, 98.93) * mm, "end": v(49.02, 99.45) * mm});
            skLineSegment(sketch, "E1093", {"start": v(49.02, 99.45) * mm, "end": v(48.68, 100) * mm});
            skLineSegment(sketch, "E1094", {"start": v(48.68, 100) * mm, "end": v(48.35, 100.55) * mm});
            skLineSegment(sketch, "E1095", {"start": v(48.35, 100.55) * mm, "end": v(48.05, 101.12) * mm});
            skLineSegment(sketch, "E1096", {"start": v(48.05, 101.12) * mm, "end": v(47.77, 101.7) * mm});
            skLineSegment(sketch, "E1097", {"start": v(47.77, 101.7) * mm, "end": v(47.5, 102.3) * mm});
            skLineSegment(sketch, "E1098", {"start": v(47.5, 102.3) * mm, "end": v(47.27, 102.92) * mm});
            skLineSegment(sketch, "E1099", {"start": v(47.27, 102.92) * mm, "end": v(47.06, 103.55) * mm});
            skArc(sketch, "E1100", {"start": v(519.25, 981.98) * mm, "mid": v(518.15, 984.63) * mm, "end": v(515.5, 985.73) * mm});
            skArc(sketch, "E1101", {"start": v(515.5, 985.73) * mm, "mid": v(512.85, 984.63) * mm, "end": v(511.75, 981.98) * mm});
            skArc(sketch, "E1102", {"start": v(511.75, 981.98) * mm, "mid": v(512.85, 979.32) * mm, "end": v(515.5, 978.23) * mm});
            skArc(sketch, "E1103", {"start": v(515.5, 978.23) * mm, "mid": v(518.15, 979.32) * mm, "end": v(519.25, 981.98) * mm});
            skArc(sketch, "E1104", {"start": v(465.74, 981.98) * mm, "mid": v(464.64, 984.63) * mm, "end": v(462, 985.73) * mm});
            skArc(sketch, "E1105", {"start": v(462, 985.73) * mm, "mid": v(459.34, 984.63) * mm, "end": v(458.24, 981.98) * mm});
            skArc(sketch, "E1106", {"start": v(458.24, 981.98) * mm, "mid": v(459.34, 979.32) * mm, "end": v(462, 978.23) * mm});
            skArc(sketch, "E1107", {"start": v(462, 978.23) * mm, "mid": v(464.64, 979.32) * mm, "end": v(465.74, 981.98) * mm});
            skArc(sketch, "E1108", {"start": v(519.25, 831.98) * mm, "mid": v(518.15, 834.63) * mm, "end": v(515.5, 835.73) * mm});
            skArc(sketch, "E1109", {"start": v(515.5, 835.73) * mm, "mid": v(512.85, 834.63) * mm, "end": v(511.75, 831.98) * mm});
            skArc(sketch, "E1110", {"start": v(511.75, 831.98) * mm, "mid": v(512.85, 829.32) * mm, "end": v(515.5, 828.23) * mm});
            skArc(sketch, "E1111", {"start": v(515.5, 828.23) * mm, "mid": v(518.15, 829.32) * mm, "end": v(519.25, 831.98) * mm});
            skArc(sketch, "E1112", {"start": v(465.74, 831.98) * mm, "mid": v(464.64, 834.63) * mm, "end": v(462, 835.73) * mm});
            skArc(sketch, "E1113", {"start": v(462, 835.73) * mm, "mid": v(459.34, 834.63) * mm, "end": v(458.24, 831.98) * mm});
            skArc(sketch, "E1114", {"start": v(458.24, 831.98) * mm, "mid": v(459.34, 829.32) * mm, "end": v(462, 828.23) * mm});
            skArc(sketch, "E1115", {"start": v(462, 828.23) * mm, "mid": v(464.64, 829.32) * mm, "end": v(465.74, 831.98) * mm});
            skArc(sketch, "E1116", {"start": v(519.25, 681.98) * mm, "mid": v(518.15, 684.63) * mm, "end": v(515.5, 685.73) * mm});
            skArc(sketch, "E1117", {"start": v(515.5, 685.73) * mm, "mid": v(512.85, 684.63) * mm, "end": v(511.75, 681.98) * mm});
            skArc(sketch, "E1118", {"start": v(511.75, 681.98) * mm, "mid": v(512.85, 679.32) * mm, "end": v(515.5, 678.23) * mm});
            skArc(sketch, "E1119", {"start": v(515.5, 678.23) * mm, "mid": v(518.15, 679.32) * mm, "end": v(519.25, 681.98) * mm});
            skArc(sketch, "E1120", {"start": v(465.74, 681.98) * mm, "mid": v(464.64, 684.63) * mm, "end": v(462, 685.73) * mm});
            skArc(sketch, "E1121", {"start": v(462, 685.73) * mm, "mid": v(459.34, 684.63) * mm, "end": v(458.24, 681.98) * mm});
            skArc(sketch, "E1122", {"start": v(458.24, 681.98) * mm, "mid": v(459.34, 679.32) * mm, "end": v(462, 678.23) * mm});
            skArc(sketch, "E1123", {"start": v(462, 678.23) * mm, "mid": v(464.64, 679.32) * mm, "end": v(465.74, 681.98) * mm});
            skArc(sketch, "E1124", {"start": v(519.25, 531.98) * mm, "mid": v(518.15, 534.63) * mm, "end": v(515.5, 535.73) * mm});
            skArc(sketch, "E1125", {"start": v(515.5, 535.73) * mm, "mid": v(512.85, 534.63) * mm, "end": v(511.75, 531.98) * mm});
            skArc(sketch, "E1126", {"start": v(511.75, 531.98) * mm, "mid": v(512.85, 529.32) * mm, "end": v(515.5, 528.23) * mm});
            skArc(sketch, "E1127", {"start": v(515.5, 528.23) * mm, "mid": v(518.15, 529.32) * mm, "end": v(519.25, 531.98) * mm});
            skArc(sketch, "E1128", {"start": v(465.74, 531.98) * mm, "mid": v(464.64, 534.63) * mm, "end": v(462, 535.73) * mm});
            skArc(sketch, "E1129", {"start": v(462, 535.73) * mm, "mid": v(459.34, 534.63) * mm, "end": v(458.24, 531.98) * mm});
            skArc(sketch, "E1130", {"start": v(458.24, 531.98) * mm, "mid": v(459.34, 529.32) * mm, "end": v(462, 528.23) * mm});
            skArc(sketch, "E1131", {"start": v(462, 528.23) * mm, "mid": v(464.64, 529.32) * mm, "end": v(465.74, 531.98) * mm});
            skArc(sketch, "E1132", {"start": v(519.25, 381.98) * mm, "mid": v(518.15, 384.63) * mm, "end": v(515.5, 385.73) * mm});
            skArc(sketch, "E1133", {"start": v(515.5, 385.73) * mm, "mid": v(512.85, 384.63) * mm, "end": v(511.75, 381.98) * mm});
            skArc(sketch, "E1134", {"start": v(511.75, 381.98) * mm, "mid": v(512.85, 379.32) * mm, "end": v(515.5, 378.23) * mm});
            skArc(sketch, "E1135", {"start": v(515.5, 378.23) * mm, "mid": v(518.15, 379.32) * mm, "end": v(519.25, 381.98) * mm});
            skArc(sketch, "E1136", {"start": v(465.74, 381.98) * mm, "mid": v(464.64, 384.63) * mm, "end": v(462, 385.73) * mm});
            skArc(sketch, "E1137", {"start": v(462, 385.73) * mm, "mid": v(459.34, 384.63) * mm, "end": v(458.24, 381.98) * mm});
            skArc(sketch, "E1138", {"start": v(458.24, 381.98) * mm, "mid": v(459.34, 379.32) * mm, "end": v(462, 378.23) * mm});
            skArc(sketch, "E1139", {"start": v(462, 378.23) * mm, "mid": v(464.64, 379.32) * mm, "end": v(465.74, 381.98) * mm});
            skArc(sketch, "E1140", {"start": v(519.25, 231.98) * mm, "mid": v(518.15, 234.63) * mm, "end": v(515.5, 235.73) * mm});
            skArc(sketch, "E1141", {"start": v(515.5, 235.73) * mm, "mid": v(512.85, 234.63) * mm, "end": v(511.75, 231.98) * mm});
            skArc(sketch, "E1142", {"start": v(511.75, 231.98) * mm, "mid": v(512.85, 229.32) * mm, "end": v(515.5, 228.23) * mm});
            skArc(sketch, "E1143", {"start": v(515.5, 228.23) * mm, "mid": v(518.15, 229.32) * mm, "end": v(519.25, 231.98) * mm});
            skArc(sketch, "E1144", {"start": v(465.74, 231.98) * mm, "mid": v(464.64, 234.63) * mm, "end": v(462, 235.73) * mm});
            skArc(sketch, "E1145", {"start": v(462, 235.73) * mm, "mid": v(459.34, 234.63) * mm, "end": v(458.24, 231.98) * mm});
            skArc(sketch, "E1146", {"start": v(458.24, 231.98) * mm, "mid": v(459.34, 229.32) * mm, "end": v(462, 228.23) * mm});
            skArc(sketch, "E1147", {"start": v(462, 228.23) * mm, "mid": v(464.64, 229.32) * mm, "end": v(465.74, 231.98) * mm});
            skArc(sketch, "E1148", {"start": v(519.25, 111.98) * mm, "mid": v(518.15, 114.63) * mm, "end": v(515.5, 115.73) * mm});
            skArc(sketch, "E1149", {"start": v(515.5, 115.73) * mm, "mid": v(512.85, 114.63) * mm, "end": v(511.75, 111.98) * mm});
            skArc(sketch, "E1150", {"start": v(511.75, 111.98) * mm, "mid": v(512.85, 109.32) * mm, "end": v(515.5, 108.23) * mm});
            skArc(sketch, "E1151", {"start": v(515.5, 108.23) * mm, "mid": v(518.15, 109.32) * mm, "end": v(519.25, 111.98) * mm});
            skArc(sketch, "E1152", {"start": v(465.74, 111.98) * mm, "mid": v(464.64, 114.63) * mm, "end": v(462, 115.73) * mm});
            skArc(sketch, "E1153", {"start": v(462, 115.73) * mm, "mid": v(459.34, 114.63) * mm, "end": v(458.24, 111.98) * mm});
            skArc(sketch, "E1154", {"start": v(458.24, 111.98) * mm, "mid": v(459.34, 109.32) * mm, "end": v(462, 108.23) * mm});
            skArc(sketch, "E1155", {"start": v(462, 108.23) * mm, "mid": v(464.64, 109.32) * mm, "end": v(465.74, 111.98) * mm});
            skArc(sketch, "E1156", {"start": v(519.25, -68.02) * mm, "mid": v(518.15, -65.37) * mm, "end": v(515.5, -64.27) * mm});
            skArc(sketch, "E1157", {"start": v(515.5, -64.27) * mm, "mid": v(512.85, -65.37) * mm, "end": v(511.75, -68.02) * mm});
            skArc(sketch, "E1158", {"start": v(511.75, -68.02) * mm, "mid": v(512.85, -70.68) * mm, "end": v(515.5, -71.77) * mm});
            skArc(sketch, "E1159", {"start": v(515.5, -71.77) * mm, "mid": v(518.15, -70.68) * mm, "end": v(519.25, -68.02) * mm});
            skArc(sketch, "E1160", {"start": v(465.74, -68.02) * mm, "mid": v(464.64, -65.37) * mm, "end": v(462, -64.27) * mm});
            skArc(sketch, "E1161", {"start": v(462, -64.27) * mm, "mid": v(459.34, -65.37) * mm, "end": v(458.24, -68.02) * mm});
            skArc(sketch, "E1162", {"start": v(458.24, -68.02) * mm, "mid": v(459.34, -70.68) * mm, "end": v(462, -71.77) * mm});
            skArc(sketch, "E1163", {"start": v(462, -71.77) * mm, "mid": v(464.64, -70.68) * mm, "end": v(465.74, -68.02) * mm});
            skArc(sketch, "E1164", {"start": v(519.25, -218.02) * mm, "mid": v(518.15, -215.37) * mm, "end": v(515.5, -214.27) * mm});
            skArc(sketch, "E1165", {"start": v(515.5, -214.27) * mm, "mid": v(512.85, -215.37) * mm, "end": v(511.75, -218.02) * mm});
            skArc(sketch, "E1166", {"start": v(511.75, -218.02) * mm, "mid": v(512.85, -220.68) * mm, "end": v(515.5, -221.77) * mm});
            skArc(sketch, "E1167", {"start": v(515.5, -221.77) * mm, "mid": v(518.15, -220.68) * mm, "end": v(519.25, -218.02) * mm});
            skArc(sketch, "E1168", {"start": v(465.74, -218.02) * mm, "mid": v(464.64, -215.37) * mm, "end": v(462, -214.27) * mm});
            skArc(sketch, "E1169", {"start": v(462, -214.27) * mm, "mid": v(459.34, -215.37) * mm, "end": v(458.24, -218.02) * mm});
            skArc(sketch, "E1170", {"start": v(458.24, -218.02) * mm, "mid": v(459.34, -220.68) * mm, "end": v(462, -221.77) * mm});
            skArc(sketch, "E1171", {"start": v(462, -221.77) * mm, "mid": v(464.64, -220.68) * mm, "end": v(465.74, -218.02) * mm});
            skArc(sketch, "E1172", {"start": v(519.25, -368.02) * mm, "mid": v(518.15, -365.37) * mm, "end": v(515.5, -364.27) * mm});
            skArc(sketch, "E1173", {"start": v(515.5, -364.27) * mm, "mid": v(512.85, -365.37) * mm, "end": v(511.75, -368.02) * mm});
            skArc(sketch, "E1174", {"start": v(511.75, -368.02) * mm, "mid": v(512.85, -370.68) * mm, "end": v(515.5, -371.77) * mm});
            skArc(sketch, "E1175", {"start": v(515.5, -371.77) * mm, "mid": v(518.15, -370.68) * mm, "end": v(519.25, -368.02) * mm});
            skArc(sketch, "E1176", {"start": v(465.74, -368.02) * mm, "mid": v(464.64, -365.37) * mm, "end": v(462, -364.27) * mm});
            skArc(sketch, "E1177", {"start": v(462, -364.27) * mm, "mid": v(459.34, -365.37) * mm, "end": v(458.24, -368.02) * mm});
            skArc(sketch, "E1178", {"start": v(458.24, -368.02) * mm, "mid": v(459.34, -370.68) * mm, "end": v(462, -371.77) * mm});
            skArc(sketch, "E1179", {"start": v(462, -371.77) * mm, "mid": v(464.64, -370.68) * mm, "end": v(465.74, -368.02) * mm});
            skArc(sketch, "E1180", {"start": v(519.25, -518.02) * mm, "mid": v(518.15, -515.37) * mm, "end": v(515.5, -514.27) * mm});
            skArc(sketch, "E1181", {"start": v(515.5, -514.27) * mm, "mid": v(512.85, -515.37) * mm, "end": v(511.75, -518.02) * mm});
            skArc(sketch, "E1182", {"start": v(511.75, -518.02) * mm, "mid": v(512.85, -520.68) * mm, "end": v(515.5, -521.77) * mm});
            skArc(sketch, "E1183", {"start": v(515.5, -521.77) * mm, "mid": v(518.15, -520.68) * mm, "end": v(519.25, -518.02) * mm});
            skArc(sketch, "E1184", {"start": v(465.74, -518.02) * mm, "mid": v(464.64, -515.37) * mm, "end": v(462, -514.27) * mm});
            skArc(sketch, "E1185", {"start": v(462, -514.27) * mm, "mid": v(459.34, -515.37) * mm, "end": v(458.24, -518.02) * mm});
            skArc(sketch, "E1186", {"start": v(458.24, -518.02) * mm, "mid": v(459.34, -520.68) * mm, "end": v(462, -521.77) * mm});
            skArc(sketch, "E1187", {"start": v(462, -521.77) * mm, "mid": v(464.64, -520.68) * mm, "end": v(465.74, -518.02) * mm});
            skArc(sketch, "E1188", {"start": v(519.25, -668.02) * mm, "mid": v(518.15, -665.37) * mm, "end": v(515.5, -664.27) * mm});
            skArc(sketch, "E1189", {"start": v(515.5, -664.27) * mm, "mid": v(512.85, -665.37) * mm, "end": v(511.75, -668.02) * mm});
            skArc(sketch, "E1190", {"start": v(511.75, -668.02) * mm, "mid": v(512.85, -670.68) * mm, "end": v(515.5, -671.77) * mm});
            skArc(sketch, "E1191", {"start": v(515.5, -671.77) * mm, "mid": v(518.15, -670.68) * mm, "end": v(519.25, -668.02) * mm});
            skArc(sketch, "E1192", {"start": v(465.74, -668.02) * mm, "mid": v(464.64, -665.37) * mm, "end": v(462, -664.27) * mm});
            skArc(sketch, "E1193", {"start": v(462, -664.27) * mm, "mid": v(459.34, -665.37) * mm, "end": v(458.24, -668.02) * mm});
            skArc(sketch, "E1194", {"start": v(458.24, -668.02) * mm, "mid": v(459.34, -670.68) * mm, "end": v(462, -671.77) * mm});
            skArc(sketch, "E1195", {"start": v(462, -671.77) * mm, "mid": v(464.64, -670.68) * mm, "end": v(465.74, -668.02) * mm});
            skArc(sketch, "E1196", {"start": v(519.25, -818.02) * mm, "mid": v(518.15, -815.37) * mm, "end": v(515.5, -814.27) * mm});
            skArc(sketch, "E1197", {"start": v(515.5, -814.27) * mm, "mid": v(512.85, -815.37) * mm, "end": v(511.75, -818.02) * mm});
            skArc(sketch, "E1198", {"start": v(511.75, -818.02) * mm, "mid": v(512.85, -820.68) * mm, "end": v(515.5, -821.77) * mm});
            skArc(sketch, "E1199", {"start": v(515.5, -821.77) * mm, "mid": v(518.15, -820.68) * mm, "end": v(519.25, -818.02) * mm});
            skArc(sketch, "E1200", {"start": v(465.74, -818.02) * mm, "mid": v(464.64, -815.37) * mm, "end": v(462, -814.27) * mm});
            skArc(sketch, "E1201", {"start": v(462, -814.27) * mm, "mid": v(459.34, -815.37) * mm, "end": v(458.24, -818.02) * mm});
            skArc(sketch, "E1202", {"start": v(458.24, -818.02) * mm, "mid": v(459.34, -820.68) * mm, "end": v(462, -821.77) * mm});
            skArc(sketch, "E1203", {"start": v(462, -821.77) * mm, "mid": v(464.64, -820.68) * mm, "end": v(465.74, -818.02) * mm});
            skArc(sketch, "E1204", {"start": v(519.25, -968.02) * mm, "mid": v(518.15, -965.37) * mm, "end": v(515.5, -964.27) * mm});
            skArc(sketch, "E1205", {"start": v(515.5, -964.27) * mm, "mid": v(512.85, -965.37) * mm, "end": v(511.75, -968.02) * mm});
            skArc(sketch, "E1206", {"start": v(511.75, -968.02) * mm, "mid": v(512.85, -970.68) * mm, "end": v(515.5, -971.77) * mm});
            skArc(sketch, "E1207", {"start": v(515.5, -971.77) * mm, "mid": v(518.15, -970.68) * mm, "end": v(519.25, -968.02) * mm});
            skArc(sketch, "E1208", {"start": v(465.74, -968.02) * mm, "mid": v(464.64, -965.37) * mm, "end": v(462, -964.27) * mm});
            skArc(sketch, "E1209", {"start": v(462, -964.27) * mm, "mid": v(459.34, -965.37) * mm, "end": v(458.24, -968.02) * mm});
            skArc(sketch, "E1210", {"start": v(458.24, -968.02) * mm, "mid": v(459.34, -970.68) * mm, "end": v(462, -971.77) * mm});
            skArc(sketch, "E1211", {"start": v(462, -971.77) * mm, "mid": v(464.64, -970.68) * mm, "end": v(465.74, -968.02) * mm});
            skArc(sketch, "E1212", {"start": v(519.25, -1118.02) * mm, "mid": v(518.15, -1115.37) * mm, "end": v(515.5, -1114.27) * mm});
            skArc(sketch, "E1213", {"start": v(515.5, -1114.27) * mm, "mid": v(512.85, -1115.37) * mm, "end": v(511.75, -1118.02) * mm});
            skArc(sketch, "E1214", {"start": v(511.75, -1118.02) * mm, "mid": v(512.85, -1120.68) * mm, "end": v(515.5, -1121.77) * mm});
            skArc(sketch, "E1215", {"start": v(515.5, -1121.77) * mm, "mid": v(518.15, -1120.68) * mm, "end": v(519.25, -1118.02) * mm});
            skArc(sketch, "E1216", {"start": v(465.74, -1118.02) * mm, "mid": v(464.64, -1115.37) * mm, "end": v(462, -1114.27) * mm});
            skArc(sketch, "E1217", {"start": v(462, -1114.27) * mm, "mid": v(459.34, -1115.37) * mm, "end": v(458.24, -1118.02) * mm});
            skArc(sketch, "E1218", {"start": v(458.24, -1118.02) * mm, "mid": v(459.34, -1120.68) * mm, "end": v(462, -1121.77) * mm});
            skArc(sketch, "E1219", {"start": v(462, -1121.77) * mm, "mid": v(464.64, -1120.68) * mm, "end": v(465.74, -1118.02) * mm});
            skArc(sketch, "E1220", {"start": v(519.25, 51.98) * mm, "mid": v(518.15, 54.63) * mm, "end": v(515.5, 55.73) * mm});
            skArc(sketch, "E1221", {"start": v(515.5, 55.73) * mm, "mid": v(512.85, 54.63) * mm, "end": v(511.75, 51.98) * mm});
            skArc(sketch, "E1222", {"start": v(511.75, 51.98) * mm, "mid": v(512.85, 49.32) * mm, "end": v(515.5, 48.23) * mm});
            skArc(sketch, "E1223", {"start": v(515.5, 48.23) * mm, "mid": v(518.15, 49.32) * mm, "end": v(519.25, 51.98) * mm});
            skArc(sketch, "E1224", {"start": v(465.74, 51.98) * mm, "mid": v(464.64, 54.63) * mm, "end": v(462, 55.73) * mm});
            skArc(sketch, "E1225", {"start": v(462, 55.73) * mm, "mid": v(459.34, 54.63) * mm, "end": v(458.24, 51.98) * mm});
            skArc(sketch, "E1226", {"start": v(458.24, 51.98) * mm, "mid": v(459.34, 49.32) * mm, "end": v(462, 48.23) * mm});
            skArc(sketch, "E1227", {"start": v(462, 48.23) * mm, "mid": v(464.64, 49.32) * mm, "end": v(465.74, 51.98) * mm});
            skArc(sketch, "E1228", {"start": v(-569.63, 981.98) * mm, "mid": v(-570.73, 984.63) * mm, "end": v(-573.38, 985.73) * mm});
            skArc(sketch, "E1229", {"start": v(-573.38, 985.73) * mm, "mid": v(-576.04, 984.63) * mm, "end": v(-577.13, 981.98) * mm});
            skArc(sketch, "E1230", {"start": v(-577.13, 981.98) * mm, "mid": v(-576.04, 979.32) * mm, "end": v(-573.38, 978.23) * mm});
            skArc(sketch, "E1231", {"start": v(-573.38, 978.23) * mm, "mid": v(-570.73, 979.32) * mm, "end": v(-569.63, 981.98) * mm});
            skArc(sketch, "E1232", {"start": v(-569.63, 831.98) * mm, "mid": v(-570.73, 834.63) * mm, "end": v(-573.38, 835.73) * mm});
            skArc(sketch, "E1233", {"start": v(-573.38, 835.73) * mm, "mid": v(-576.04, 834.63) * mm, "end": v(-577.13, 831.98) * mm});
            skArc(sketch, "E1234", {"start": v(-577.13, 831.98) * mm, "mid": v(-576.04, 829.32) * mm, "end": v(-573.38, 828.23) * mm});
            skArc(sketch, "E1235", {"start": v(-573.38, 828.23) * mm, "mid": v(-570.73, 829.32) * mm, "end": v(-569.63, 831.98) * mm});
            skArc(sketch, "E1236", {"start": v(-569.63, 681.98) * mm, "mid": v(-570.73, 684.63) * mm, "end": v(-573.38, 685.73) * mm});
            skArc(sketch, "E1237", {"start": v(-573.38, 685.73) * mm, "mid": v(-576.04, 684.63) * mm, "end": v(-577.13, 681.98) * mm});
            skArc(sketch, "E1238", {"start": v(-577.13, 681.98) * mm, "mid": v(-576.04, 679.32) * mm, "end": v(-573.38, 678.23) * mm});
            skArc(sketch, "E1239", {"start": v(-573.38, 678.23) * mm, "mid": v(-570.73, 679.32) * mm, "end": v(-569.63, 681.98) * mm});
            skArc(sketch, "E1240", {"start": v(-569.63, 531.98) * mm, "mid": v(-570.73, 534.63) * mm, "end": v(-573.38, 535.73) * mm});
            skArc(sketch, "E1241", {"start": v(-573.38, 535.73) * mm, "mid": v(-576.04, 534.63) * mm, "end": v(-577.13, 531.98) * mm});
            skArc(sketch, "E1242", {"start": v(-577.13, 531.98) * mm, "mid": v(-576.04, 529.32) * mm, "end": v(-573.38, 528.23) * mm});
            skArc(sketch, "E1243", {"start": v(-573.38, 528.23) * mm, "mid": v(-570.73, 529.32) * mm, "end": v(-569.63, 531.98) * mm});
            skArc(sketch, "E1244", {"start": v(-569.63, 381.98) * mm, "mid": v(-570.73, 384.63) * mm, "end": v(-573.38, 385.73) * mm});
            skArc(sketch, "E1245", {"start": v(-573.38, 385.73) * mm, "mid": v(-576.04, 384.63) * mm, "end": v(-577.13, 381.98) * mm});
            skArc(sketch, "E1246", {"start": v(-577.13, 381.98) * mm, "mid": v(-576.04, 379.32) * mm, "end": v(-573.38, 378.23) * mm});
            skArc(sketch, "E1247", {"start": v(-573.38, 378.23) * mm, "mid": v(-570.73, 379.32) * mm, "end": v(-569.63, 381.98) * mm});
            skArc(sketch, "E1248", {"start": v(-569.63, 231.98) * mm, "mid": v(-570.73, 234.63) * mm, "end": v(-573.38, 235.73) * mm});
            skArc(sketch, "E1249", {"start": v(-573.38, 235.73) * mm, "mid": v(-576.04, 234.63) * mm, "end": v(-577.13, 231.98) * mm});
            skArc(sketch, "E1250", {"start": v(-577.13, 231.98) * mm, "mid": v(-576.04, 229.32) * mm, "end": v(-573.38, 228.23) * mm});
            skArc(sketch, "E1251", {"start": v(-573.38, 228.23) * mm, "mid": v(-570.73, 229.32) * mm, "end": v(-569.63, 231.98) * mm});
            skArc(sketch, "E1252", {"start": v(-569.63, 111.98) * mm, "mid": v(-570.73, 114.63) * mm, "end": v(-573.38, 115.73) * mm});
            skArc(sketch, "E1253", {"start": v(-573.38, 115.73) * mm, "mid": v(-576.04, 114.63) * mm, "end": v(-577.13, 111.98) * mm});
            skArc(sketch, "E1254", {"start": v(-577.13, 111.98) * mm, "mid": v(-576.04, 109.32) * mm, "end": v(-573.38, 108.23) * mm});
            skArc(sketch, "E1255", {"start": v(-573.38, 108.23) * mm, "mid": v(-570.73, 109.32) * mm, "end": v(-569.63, 111.98) * mm});
            skArc(sketch, "E1256", {"start": v(-569.63, -68.02) * mm, "mid": v(-570.73, -65.37) * mm, "end": v(-573.38, -64.27) * mm});
            skArc(sketch, "E1257", {"start": v(-573.38, -64.27) * mm, "mid": v(-576.04, -65.37) * mm, "end": v(-577.13, -68.02) * mm});
            skArc(sketch, "E1258", {"start": v(-577.13, -68.02) * mm, "mid": v(-576.04, -70.68) * mm, "end": v(-573.38, -71.77) * mm});
            skArc(sketch, "E1259", {"start": v(-573.38, -71.77) * mm, "mid": v(-570.73, -70.68) * mm, "end": v(-569.63, -68.02) * mm});
            skArc(sketch, "E1260", {"start": v(-569.63, -218.02) * mm, "mid": v(-570.73, -215.37) * mm, "end": v(-573.38, -214.27) * mm});
            skArc(sketch, "E1261", {"start": v(-573.38, -214.27) * mm, "mid": v(-576.04, -215.37) * mm, "end": v(-577.13, -218.02) * mm});
            skArc(sketch, "E1262", {"start": v(-577.13, -218.02) * mm, "mid": v(-576.04, -220.68) * mm, "end": v(-573.38, -221.77) * mm});
            skArc(sketch, "E1263", {"start": v(-573.38, -221.77) * mm, "mid": v(-570.73, -220.68) * mm, "end": v(-569.63, -218.02) * mm});
            skArc(sketch, "E1264", {"start": v(-569.63, -368.02) * mm, "mid": v(-570.73, -365.37) * mm, "end": v(-573.38, -364.27) * mm});
            skArc(sketch, "E1265", {"start": v(-573.38, -364.27) * mm, "mid": v(-576.04, -365.37) * mm, "end": v(-577.13, -368.02) * mm});
            skArc(sketch, "E1266", {"start": v(-577.13, -368.02) * mm, "mid": v(-576.04, -370.68) * mm, "end": v(-573.38, -371.77) * mm});
            skArc(sketch, "E1267", {"start": v(-573.38, -371.77) * mm, "mid": v(-570.73, -370.68) * mm, "end": v(-569.63, -368.02) * mm});
            skArc(sketch, "E1268", {"start": v(-569.63, -518.02) * mm, "mid": v(-570.73, -515.37) * mm, "end": v(-573.38, -514.27) * mm});
            skArc(sketch, "E1269", {"start": v(-573.38, -514.27) * mm, "mid": v(-576.04, -515.37) * mm, "end": v(-577.13, -518.02) * mm});
            skArc(sketch, "E1270", {"start": v(-577.13, -518.02) * mm, "mid": v(-576.04, -520.68) * mm, "end": v(-573.38, -521.77) * mm});
            skArc(sketch, "E1271", {"start": v(-573.38, -521.77) * mm, "mid": v(-570.73, -520.68) * mm, "end": v(-569.63, -518.02) * mm});
            skArc(sketch, "E1272", {"start": v(-569.63, -668.02) * mm, "mid": v(-570.73, -665.37) * mm, "end": v(-573.38, -664.27) * mm});
            skArc(sketch, "E1273", {"start": v(-573.38, -664.27) * mm, "mid": v(-576.04, -665.37) * mm, "end": v(-577.13, -668.02) * mm});
            skArc(sketch, "E1274", {"start": v(-577.13, -668.02) * mm, "mid": v(-576.04, -670.68) * mm, "end": v(-573.38, -671.77) * mm});
            skArc(sketch, "E1275", {"start": v(-573.38, -671.77) * mm, "mid": v(-570.73, -670.68) * mm, "end": v(-569.63, -668.02) * mm});
            skArc(sketch, "E1276", {"start": v(-569.63, -818.02) * mm, "mid": v(-570.73, -815.37) * mm, "end": v(-573.38, -814.27) * mm});
            skArc(sketch, "E1277", {"start": v(-573.38, -814.27) * mm, "mid": v(-576.04, -815.37) * mm, "end": v(-577.13, -818.02) * mm});
            skArc(sketch, "E1278", {"start": v(-577.13, -818.02) * mm, "mid": v(-576.04, -820.68) * mm, "end": v(-573.38, -821.77) * mm});
            skArc(sketch, "E1279", {"start": v(-573.38, -821.77) * mm, "mid": v(-570.73, -820.68) * mm, "end": v(-569.63, -818.02) * mm});
            skArc(sketch, "E1280", {"start": v(-569.63, -968.02) * mm, "mid": v(-570.73, -965.37) * mm, "end": v(-573.38, -964.27) * mm});
            skArc(sketch, "E1281", {"start": v(-573.38, -964.27) * mm, "mid": v(-576.04, -965.37) * mm, "end": v(-577.13, -968.02) * mm});
            skArc(sketch, "E1282", {"start": v(-577.13, -968.02) * mm, "mid": v(-576.04, -970.68) * mm, "end": v(-573.38, -971.77) * mm});
            skArc(sketch, "E1283", {"start": v(-573.38, -971.77) * mm, "mid": v(-570.73, -970.68) * mm, "end": v(-569.63, -968.02) * mm});
            skArc(sketch, "E1284", {"start": v(-569.63, -1118.02) * mm, "mid": v(-570.73, -1115.37) * mm, "end": v(-573.38, -1114.27) * mm});
            skArc(sketch, "E1285", {"start": v(-573.38, -1114.27) * mm, "mid": v(-576.04, -1115.37) * mm, "end": v(-577.13, -1118.02) * mm});
            skArc(sketch, "E1286", {"start": v(-577.13, -1118.02) * mm, "mid": v(-576.04, -1120.68) * mm, "end": v(-573.38, -1121.77) * mm});
            skArc(sketch, "E1287", {"start": v(-573.38, -1121.77) * mm, "mid": v(-570.73, -1120.68) * mm, "end": v(-569.63, -1118.02) * mm});
            skArc(sketch, "E1288", {"start": v(-569.63, 51.98) * mm, "mid": v(-570.73, 54.63) * mm, "end": v(-573.38, 55.73) * mm});
            skArc(sketch, "E1289", {"start": v(-573.38, 55.73) * mm, "mid": v(-576.04, 54.63) * mm, "end": v(-577.13, 51.98) * mm});
            skArc(sketch, "E1290", {"start": v(-577.13, 51.98) * mm, "mid": v(-576.04, 49.32) * mm, "end": v(-573.38, 48.23) * mm});
            skArc(sketch, "E1291", {"start": v(-573.38, 48.23) * mm, "mid": v(-570.73, 49.32) * mm, "end": v(-569.63, 51.98) * mm});
            skArc(sketch, "E1292", {"start": v(-51.03, -1121.87) * mm, "mid": v(-53.69, -1122.97) * mm, "end": v(-54.78, -1125.62) * mm});
            skArc(sketch, "E1293", {"start": v(-54.78, -1125.62) * mm, "mid": v(-53.69, -1128.27) * mm, "end": v(-51.03, -1129.37) * mm});
            skArc(sketch, "E1294", {"start": v(-51.03, -1129.37) * mm, "mid": v(-48.38, -1128.27) * mm, "end": v(-47.28, -1125.62) * mm});
            skArc(sketch, "E1295", {"start": v(-47.28, -1125.62) * mm, "mid": v(-48.38, -1122.97) * mm, "end": v(-51.03, -1121.87) * mm});
            skArc(sketch, "E1296", {"start": v(-58.55, -642.93) * mm, "mid": v(-61.2, -644.03) * mm, "end": v(-62.3, -646.68) * mm});
            skArc(sketch, "E1297", {"start": v(-62.3, -646.68) * mm, "mid": v(-61.2, -649.33) * mm, "end": v(-58.55, -650.43) * mm});
            skArc(sketch, "E1298", {"start": v(-58.55, -650.43) * mm, "mid": v(-55.9, -649.33) * mm, "end": v(-54.8, -646.68) * mm});
            skArc(sketch, "E1299", {"start": v(-54.8, -646.68) * mm, "mid": v(-55.9, -644.03) * mm, "end": v(-58.55, -642.93) * mm});
            skArc(sketch, "E1300", {"start": v(-54.8, -10.25) * mm, "mid": v(-57.44, -11.35) * mm, "end": v(-58.54, -14) * mm});
            skArc(sketch, "E1301", {"start": v(-58.54, -14) * mm, "mid": v(-57.44, -16.65) * mm, "end": v(-54.8, -17.75) * mm});
            skArc(sketch, "E1302", {"start": v(-54.8, -17.75) * mm, "mid": v(-52.14, -16.65) * mm, "end": v(-51.04, -14) * mm});
            skArc(sketch, "E1303", {"start": v(-51.04, -14) * mm, "mid": v(-52.14, -11.35) * mm, "end": v(-54.8, -10.25) * mm});
            skArc(sketch, "E1304", {"start": v(-54.8, 477.97) * mm, "mid": v(-57.44, 476.87) * mm, "end": v(-58.54, 474.22) * mm});
            skArc(sketch, "E1305", {"start": v(-58.54, 474.22) * mm, "mid": v(-57.44, 471.56) * mm, "end": v(-54.8, 470.47) * mm});
            skArc(sketch, "E1306", {"start": v(-54.8, 470.47) * mm, "mid": v(-52.14, 471.56) * mm, "end": v(-51.04, 474.22) * mm});
            skArc(sketch, "E1307", {"start": v(-51.04, 474.22) * mm, "mid": v(-52.14, 476.87) * mm, "end": v(-54.8, 477.97) * mm});
            skArc(sketch, "E1308", {"start": v(-58.55, 932.38) * mm, "mid": v(-61.2, 931.28) * mm, "end": v(-62.3, 928.63) * mm});
            skArc(sketch, "E1309", {"start": v(-62.3, 928.63) * mm, "mid": v(-61.2, 925.98) * mm, "end": v(-58.55, 924.88) * mm});
            skArc(sketch, "E1310", {"start": v(-58.55, 924.88) * mm, "mid": v(-55.9, 925.98) * mm, "end": v(-54.8, 928.63) * mm});
            skArc(sketch, "E1311", {"start": v(-54.8, 928.63) * mm, "mid": v(-55.9, 931.28) * mm, "end": v(-58.55, 932.38) * mm});
            skSolve(sketch);
        }
        {
            var Q0;
            {var subQ4=sQuery(id+"F0.wireOp",EDGE,"E4");Q0=makeQuery(id+"F0.imprint","IMPRINT",FACE,{"disambiguationData":[TD([[makeQuery(id+"F0.imprint","IMPRINT",EDGE,{"derivedFrom":subQ4}),1.0]])]});}
            var Q1;
            Q1=makeQuery(id+"F0.imprint","IMPRINT",FACE,{"disambiguationData":[TD([[makeQuery(id+"F0.imprint","IMPRINT",EDGE,{"derivedFrom":sQuery(id+"F0.wireOp",EDGE,"E361")}),-1.0]])]});
            var Q2;
            Q2=makeQuery(id+"F0.imprint","IMPRINT",FACE,{"disambiguationData":[TD([[makeQuery(id+"F0.imprint","IMPRINT",EDGE,{"derivedFrom":sQuery(id+"F0.wireOp",EDGE,"E617")}),-1.0]])]});
            var Q3;
            {var subQ0=sQuery(id+"F0.wireOp",EDGE,"E247");Q3=makeQuery(id+"F0.imprint","IMPRINT",FACE,{"disambiguationData":[TD([[makeQuery(id+"F0.imprint","IMPRINT",EDGE,{"derivedFrom":subQ0}),-1.0]])]});}
            extrude(context, id + "F1", {"entities" : qUnion([Q0, Q1, Q2, Q3]), "depth" : 18 * mm});
        }
    });
